FCSTD DOCUMENT  (FreeCAD 0.20R29603 (Git))
Label: layout
License: All rights reserved
LicenseURL: http://en.wikipedia.org/wiki/All_rights_reserved
objects: Sketcher::SketchObject×6
note: 6 computed .brp shape members not serialized (recipe doc carries the construction recipe); baked Part::Feature solids carry a one-line shape summary decoded from their .brp

FEATURE [Sketcher::SketchObject] Sketch  label="grid"
  FullyConstrained = true
  sketch-geometry (158):
    g0: LineSegment StartX=-9 StartY=8.5 StartZ=0 EndX=9 EndY=8.5 EndZ=0
    g1: LineSegment StartX=9 StartY=8.5 StartZ=0 EndX=9 EndY=-8.5 EndZ=0
    g2: LineSegment StartX=9 StartY=-8.5 StartZ=0 EndX=-9 EndY=-8.5 EndZ=0
    g3: LineSegment StartX=-9 StartY=-8.5 StartZ=0 EndX=-9 EndY=8.5 EndZ=0
    g4: LineSegment StartX=-28.0528 StartY=-14.2521 StartZ=0 EndX=-10.1213 EndY=-12.6833 EndZ=0
    g5: LineSegment StartX=-28.0528 StartY=-14.2521 StartZ=0 EndX=-29.5345 EndY=2.68325 EndZ=0
    g6: LineSegment StartX=-29.5345 StartY=2.68325 StartZ=0 EndX=-11.603 EndY=4.25206 EndZ=0
    g7: LineSegment StartX=-11.603 StartY=4.25206 StartZ=0 EndX=-10.1213 EndY=-12.6833 EndZ=0
    g8: GeomPoint X=-19.8279 Y=-5 Z=0
    g9: LineSegment StartX=9 StartY=25.5 StartZ=0 EndX=-9 EndY=25.5 EndZ=0
    g10: LineSegment StartX=-9 StartY=25.5 StartZ=0 EndX=-9 EndY=8.5 EndZ=0
    g11: LineSegment StartX=-9 StartY=8.5 StartZ=0 EndX=9 EndY=8.5 EndZ=0
    g12: LineSegment StartX=9 StartY=8.5 StartZ=0 EndX=9 EndY=25.5 EndZ=0
    g13: LineSegment StartX=-9 StartY=-8.5 StartZ=0 EndX=9 EndY=-8.5 EndZ=0
    g14: LineSegment StartX=9 StartY=-8.5 StartZ=0 EndX=9 EndY=-25.5 EndZ=0
    g15: LineSegment StartX=9 StartY=-25.5 StartZ=0 EndX=-9 EndY=-25.5 EndZ=0
    g16: LineSegment StartX=-9 StartY=-25.5 StartZ=0 EndX=-9 EndY=-8.5 EndZ=0
    g17: LineSegment StartX=-10.1213 StartY=-12.6833 StartZ=0 EndX=-8.63967 EndY=-29.6186 EndZ=0
    g18: LineSegment StartX=-8.63967 StartY=-29.6186 StartZ=0 EndX=-26.5712 EndY=-31.1874 EndZ=0
    g19: LineSegment StartX=-26.5712 StartY=-31.1874 StartZ=0 EndX=-28.0528 EndY=-14.2521 EndZ=0
    g20: LineSegment StartX=9 StartY=42.5 StartZ=0 EndX=-9 EndY=42.5 EndZ=0
    g21: LineSegment StartX=-9 StartY=42.5 StartZ=0 EndX=-9 EndY=25.5 EndZ=0
    g22: LineSegment StartX=-9 StartY=25.5 StartZ=0 EndX=9 EndY=25.5 EndZ=0
    g23: LineSegment StartX=9 StartY=25.5 StartZ=0 EndX=9 EndY=42.5 EndZ=0
    g24: LineSegment StartX=-11.603 StartY=4.25206 StartZ=0 EndX=-13.0846 EndY=21.1874 EndZ=0
    g25: LineSegment StartX=-13.0846 StartY=21.1874 StartZ=0 EndX=-31.0161 EndY=19.6186 EndZ=0
    g26: LineSegment StartX=-29.5345 StartY=2.68325 StartZ=0 EndX=-31.0161 EndY=19.6186 EndZ=0
    g27: LineSegment StartX=-13.0846 StartY=21.1874 StartZ=0 EndX=-14.5663 EndY=38.1227 EndZ=0
    g28: LineSegment StartX=-14.5663 StartY=38.1227 StartZ=0 EndX=-32.4978 EndY=36.5539 EndZ=0
    g29: LineSegment StartX=-32.4978 StartY=36.5539 StartZ=0 EndX=-31.0161 EndY=19.6186 EndZ=0
    g30: GeomPoint X=-22.7912 Y=28.8706 Z=0
    g31: GeomPoint X=-21.3095 Y=11.9353 Z=0
    g32: GeomPoint X=-18.3462 Y=-21.9353 Z=0
    g33: LineSegment StartX=11.603 StartY=4.25206 StartZ=0 EndX=29.5345 EndY=2.68325 EndZ=0
    g34: LineSegment StartX=29.5345 StartY=2.68325 StartZ=0 EndX=28.0528 EndY=-14.2521 EndZ=0
    g35: LineSegment StartX=28.0528 StartY=-14.2521 StartZ=0 EndX=10.1213 EndY=-12.6833 EndZ=0
    g36: LineSegment StartX=10.1213 StartY=-12.6833 StartZ=0 EndX=11.603 EndY=4.25206 EndZ=0
    g37: GeomPoint X=19.8279 Y=-5 Z=0
    g38: LineSegment StartX=28.0528 StartY=-14.2521 StartZ=0 EndX=26.5712 EndY=-31.1874 EndZ=0
    g39: LineSegment StartX=26.5712 StartY=-31.1874 StartZ=0 EndX=8.63967 EndY=-29.6186 EndZ=0
    g40: LineSegment StartX=8.63967 StartY=-29.6186 StartZ=0 EndX=10.1213 EndY=-12.6833 EndZ=0
    g41: GeomPoint X=18.3462 Y=-21.9353 Z=0
    g42: LineSegment StartX=29.5345 StartY=2.68325 StartZ=0 EndX=31.0161 EndY=19.6186 EndZ=0
    g43: LineSegment StartX=31.0161 StartY=19.6186 StartZ=0 EndX=13.0846 EndY=21.1874 EndZ=0
    g44: LineSegment StartX=13.0846 StartY=21.1874 StartZ=0 EndX=11.603 EndY=4.25206 EndZ=0
    g45: GeomPoint X=21.3095 Y=11.9353 Z=0
    g46: LineSegment StartX=31.0161 StartY=19.6186 StartZ=0 EndX=32.4978 EndY=36.5539 EndZ=0
    g47: LineSegment StartX=32.4978 StartY=36.5539 StartZ=0 EndX=14.5663 EndY=38.1227 EndZ=0
    g48: LineSegment StartX=14.5663 StartY=38.1227 StartZ=0 EndX=13.0846 EndY=21.1874 EndZ=0
    g49: GeomPoint X=22.7912 Y=28.8706 Z=0
    g50: LineSegment StartX=-26.5712 StartY=-31.1874 StartZ=0 EndX=-44.5027 EndY=-32.7562 EndZ=0
    g51: LineSegment StartX=-44.5027 StartY=-32.7562 StartZ=0 EndX=-45.9843 EndY=-15.8209 EndZ=0
    g52: LineSegment StartX=-45.9843 StartY=-15.8209 StartZ=0 EndX=-28.0528 EndY=-14.2521 EndZ=0
    g53: GeomPoint X=-36.2778 Y=-23.5041 Z=0
    g54: LineSegment StartX=-29.5345 StartY=2.68325 StartZ=0 EndX=-47.466 EndY=1.11445 EndZ=0
    g55: LineSegment StartX=-47.466 StartY=1.11445 StartZ=0 EndX=-45.9843 EndY=-15.8209 EndZ=0
    g56: LineSegment StartX=-31.0161 StartY=19.6186 StartZ=0 EndX=-48.9476 EndY=18.0498 EndZ=0
    g57: LineSegment StartX=-48.9476 StartY=18.0498 StartZ=0 EndX=-47.466 EndY=1.11445 EndZ=0
    g58: LineSegment StartX=-48.9476 StartY=18.0498 StartZ=0 EndX=-50.4293 EndY=34.9851 EndZ=0
    g59: LineSegment StartX=-50.4293 StartY=34.9851 StartZ=0 EndX=-32.4978 EndY=36.5539 EndZ=0
    g60: GeomPoint X=-40.7227 Y=27.3018 Z=0
    g61: GeomPoint X=-39.241 Y=10.3665 Z=0
    g62: GeomPoint X=-37.7594 Y=-6.5688 Z=0
    g63: LineSegment StartX=30.8244 StartY=-7.0663 StartZ=0 EndX=27.8724 EndY=-23.808 EndZ=0
    g64: LineSegment StartX=27.8724 StartY=-23.808 StartZ=0 EndX=45.5989 EndY=-26.9337 EndZ=0
    g65: LineSegment StartX=45.5989 StartY=-26.9337 StartZ=0 EndX=48.5509 EndY=-10.192 EndZ=0
    g66: LineSegment StartX=48.5509 StartY=-10.192 StartZ=0 EndX=30.8244 EndY=-7.0663 EndZ=0
    g67: GeomPoint X=38.2116 Y=-17 Z=0
    g68: LineSegment StartX=45.5989 StartY=-26.9337 StartZ=0 EndX=42.6469 EndY=-43.6754 EndZ=0
    g69: LineSegment StartX=42.6469 StartY=-43.6754 StartZ=0 EndX=24.9203 EndY=-40.5498 EndZ=0
    g70: LineSegment StartX=24.9203 StartY=-40.5498 StartZ=0 EndX=27.8724 EndY=-23.808 EndZ=0
    g71: GeomPoint X=35.2596 Y=-33.7417 Z=0
    g72: LineSegment StartX=48.5509 StartY=-10.192 StartZ=0 EndX=51.5029 EndY=6.54976 EndZ=0
    g73: LineSegment StartX=51.5029 StartY=6.54976 StartZ=0 EndX=33.7764 EndY=9.67543 EndZ=0
    g74: LineSegment StartX=33.7764 StartY=9.67543 StartZ=0 EndX=30.8244 EndY=-7.0663 EndZ=0
    g75: GeomPoint X=41.1637 Y=-0.258268 Z=0
    g76: LineSegment StartX=51.5029 StartY=6.54976 StartZ=0 EndX=54.4549 EndY=23.2915 EndZ=0
    g77: LineSegment StartX=54.4549 StartY=23.2915 StartZ=0 EndX=36.7284 EndY=26.4172 EndZ=0
    g78: LineSegment StartX=36.7284 StartY=26.4172 StartZ=0 EndX=33.7764 EndY=9.67543 EndZ=0
    g79: GeomPoint X=44.1157 Y=16.4835 Z=0
    g80: LineSegment StartX=42.6469 StartY=-43.6754 StartZ=0 EndX=60.3734 EndY=-46.8011 EndZ=0
    g81: LineSegment StartX=60.3734 StartY=-46.8011 StartZ=0 EndX=63.3254 EndY=-30.0594 EndZ=0
    g82: LineSegment StartX=63.3254 StartY=-30.0594 StartZ=0 EndX=45.5989 EndY=-26.9337 EndZ=0
    g83: GeomPoint X=52.9862 Y=-36.8674 Z=0
    g84: LineSegment StartX=63.3254 StartY=-30.0594 StartZ=0 EndX=66.2775 EndY=-13.3176 EndZ=0
    g85: LineSegment StartX=48.5509 StartY=-10.192 StartZ=0 EndX=66.2775 EndY=-13.3176 EndZ=0
    g86: GeomPoint X=55.9382 Y=-20.1257 Z=0
    g87: LineSegment StartX=66.2775 StartY=-13.3176 StartZ=0 EndX=69.2295 EndY=3.4241 EndZ=0
    g88: LineSegment StartX=69.2295 StartY=3.4241 StartZ=0 EndX=51.5029 EndY=6.54976 EndZ=0
    g89: LineSegment StartX=72.1815 StartY=20.1658 StartZ=0 EndX=54.4549 EndY=23.2915 EndZ=0
    g90: GeomPoint X=58.8902 Y=-3.38394 Z=0
    g91: GeomPoint X=61.8422 Y=13.3578 Z=0
    g92: GeomPoint X=80.4064 Y=10.9138 Z=0
    g93: GeomPoint X=78.9248 Y=-6.02154 Z=0
    g94: LineSegment StartX=108.044 StartY=17.0282 StartZ=0 EndX=106.563 EndY=0.0929121 EndZ=0
    g95: GeomPoint X=98.3379 Y=9.34497 Z=0
    g96: GeomPoint X=96.8563 Y=-7.59034 Z=0
    g97: LineSegment StartX=-20.4485 StartY=-30.846 StartZ=0 EndX=-37.8352 EndY=-35.5048 EndZ=0
    g98: LineSegment StartX=-37.8352 StartY=-35.5048 StartZ=0 EndX=-33.4353 EndY=-51.9255 EndZ=0
    g99: LineSegment StartX=-33.4353 StartY=-51.9255 StartZ=0 EndX=-16.0486 EndY=-47.2668 EndZ=0
    g100: LineSegment StartX=-16.0486 StartY=-47.2668 StartZ=0 EndX=-20.4485 EndY=-30.846 EndZ=0
    g101: LineSegment StartX=-41.9353 StartY=-37.2031 StartZ=0 EndX=-57.5237 EndY=-46.2031 EndZ=0
    g102: LineSegment StartX=-57.5237 StartY=-46.2031 StartZ=0 EndX=-49.0237 EndY=-60.9255 EndZ=0
    g103: LineSegment StartX=-49.0237 StartY=-60.9255 StartZ=0 EndX=-33.4353 EndY=-51.9255 EndZ=0
    g104: LineSegment StartX=-33.4353 StartY=-51.9255 StartZ=0 EndX=-41.9353 EndY=-37.2031 EndZ=0
    g105: LineSegment StartX=-16.0486 StartY=-30.2668 StartZ=0 EndX=1.9514 EndY=-30.2668 EndZ=0
    g106: LineSegment StartX=-16.0486 StartY=-47.2668 StartZ=0 EndX=-16.0486 EndY=-30.2668 EndZ=0
    g107: GeomPoint X=-26.9419 Y=-41.3858 Z=0
    g108: GeomPoint X=-45.4795 Y=-49.0643 Z=0
    g109: GeomPoint X=-53.9795 Y=-34.3419 Z=0
    g110: LineSegment StartX=-41.9353 StartY=-37.2031 StartZ=0 EndX=-50.4353 EndY=-22.4806 EndZ=0
    g111: LineSegment StartX=-50.4353 StartY=-22.4806 StartZ=0 EndX=-66.0237 EndY=-31.4806 EndZ=0
    g112: LineSegment StartX=-66.0237 StartY=-31.4806 StartZ=0 EndX=-57.5237 EndY=-46.2031 EndZ=0
    g113: LineSegment StartX=1.9514 StartY=-47.2668 StartZ=0 EndX=-16.0486 EndY=-47.2668 EndZ=0
    g114: LineSegment StartX=72.1815 StartY=20.1658 StartZ=0 EndX=69.2295 EndY=3.4241 EndZ=0
    g115: LineSegment StartX=72.1815 StartY=20.1658 StartZ=0 EndX=90.113 EndY=18.597 EndZ=0
    g116: LineSegment StartX=72.1815 StartY=20.1658 StartZ=0 EndX=70.6998 EndY=3.23052 EndZ=0
    g117: LineSegment StartX=90.113 StartY=18.597 StartZ=0 EndX=88.6313 EndY=1.66172 EndZ=0
    g118: LineSegment StartX=88.6313 StartY=1.66172 StartZ=0 EndX=70.6998 EndY=3.23052 EndZ=0
    g119: LineSegment StartX=108.044 StartY=17.0282 StartZ=0 EndX=90.113 EndY=18.597 EndZ=0
    g120: LineSegment StartX=106.563 StartY=0.0929121 StartZ=0 EndX=88.6313 EndY=1.66172 EndZ=0
    g121: LineSegment StartX=108.044 StartY=17.0282 StartZ=0 EndX=125.976 EndY=15.4594 EndZ=0
    g122: LineSegment StartX=125.976 StartY=15.4594 StartZ=0 EndX=124.494 EndY=-1.47589 EndZ=0
    g123: LineSegment StartX=124.494 StartY=-1.47589 StartZ=0 EndX=106.563 EndY=0.0929121 EndZ=0
    g124: GeomPoint X=116.269 Y=7.77617 Z=0
    g125: LineSegment StartX=70.6998 StartY=3.23052 StartZ=0 EndX=69.2182 EndY=-13.7048 EndZ=0
    g126: LineSegment StartX=88.6313 StartY=1.66172 StartZ=0 EndX=87.1497 EndY=-15.2736 EndZ=0
    g127: LineSegment StartX=87.1497 StartY=-15.2736 StartZ=0 EndX=69.2182 EndY=-13.7048 EndZ=0
    g128: LineSegment StartX=106.563 StartY=0.0929121 StartZ=0 EndX=105.081 EndY=-16.8424 EndZ=0
    g129: LineSegment StartX=105.081 StartY=-16.8424 StartZ=0 EndX=87.1497 EndY=-15.2736 EndZ=0
    g130: LineSegment StartX=124.494 StartY=-1.47589 StartZ=0 EndX=123.013 EndY=-18.4112 EndZ=0
    g131: LineSegment StartX=123.013 StartY=-18.4112 StartZ=0 EndX=105.081 EndY=-16.8424 EndZ=0
    g132: GeomPoint X=114.788 Y=-9.15914 Z=0
    g133: LineSegment StartX=69.2182 StartY=-13.7048 StartZ=0 EndX=67.7365 EndY=-30.6401 EndZ=0
    g134: LineSegment StartX=67.7365 StartY=-30.6401 StartZ=0 EndX=85.6681 EndY=-32.2089 EndZ=0
    g135: LineSegment StartX=87.1497 StartY=-15.2736 StartZ=0 EndX=85.6681 EndY=-32.2089 EndZ=0
    g136: LineSegment StartX=105.081 StartY=-16.8424 StartZ=0 EndX=103.6 EndY=-33.7777 EndZ=0
    g137: LineSegment StartX=103.6 StartY=-33.7777 StartZ=0 EndX=85.6681 EndY=-32.2089 EndZ=0
    g138: LineSegment StartX=123.013 StartY=-18.4112 StartZ=0 EndX=121.531 EndY=-35.3465 EndZ=0
    g139: LineSegment StartX=121.531 StartY=-35.3465 StartZ=0 EndX=103.6 EndY=-33.7777 EndZ=0
    g140: GeomPoint X=113.306 Y=-26.0945 Z=0
    g141: GeomPoint X=95.3746 Y=-24.5257 Z=0
    g142: GeomPoint X=77.4431 Y=-22.9568 Z=0
    g143: LineSegment StartX=67.7365 StartY=-30.6401 StartZ=0 EndX=66.2549 EndY=-47.5754 EndZ=0
    g144: LineSegment StartX=85.6681 StartY=-32.2089 StartZ=0 EndX=84.1864 EndY=-49.1442 EndZ=0
    g145: LineSegment StartX=66.2549 StartY=-47.5754 StartZ=0 EndX=84.1864 EndY=-49.1442 EndZ=0
    g146: LineSegment StartX=103.6 StartY=-33.7777 StartZ=0 EndX=102.118 EndY=-50.713 EndZ=0
    g147: LineSegment StartX=102.118 StartY=-50.713 StartZ=0 EndX=84.1864 EndY=-49.1442 EndZ=0
    g148: LineSegment StartX=102.118 StartY=-50.713 StartZ=0 EndX=120.049 EndY=-52.2818 EndZ=0
    g149: LineSegment StartX=121.531 StartY=-35.3465 StartZ=0 EndX=120.049 EndY=-52.2818 EndZ=0
    g150: GeomPoint X=75.9615 Y=-39.8922 Z=0
    g151: GeomPoint X=93.893 Y=-41.461 Z=0
    g152: GeomPoint X=111.824 Y=-43.0298 Z=0
    g153: GeomPoint X=-1e-16 Y=17 Z=0
    g154: GeomPoint X=7e-16 Y=34 Z=0
    g155: GeomPoint X=-2e-16 Y=-17 Z=0
    g156: LineSegment StartX=1.9514 StartY=-47.2668 StartZ=0 EndX=1.9514 EndY=-30.2668 EndZ=0
    g157: GeomPoint X=-7.0486 Y=-38.7668 Z=0
  constraints (360):
    c: Coincident(g0,g1)
    c: Coincident(g1,g2)
    c: Coincident(g2,g3)
    c: Coincident(g3,g0)
    c: Horizontal(g0)
    c: Horizontal(g2)
    c: Vertical(g1)
    c: Vertical(g3)
    c: Distance(g0) = 18
    c: Distance(g1) = 17
    c: Symmetric(g0,g1,g-1)
    c: Coincident(g5,g4)
    c: Coincident(g6,g5)
    c: Coincident(g7,g6)
    c: Coincident(g7,g4)
    c: Perpendicular(g4,g5)
    c: Perpendicular(g4,g7)
    c: Perpendicular(g6,g7)
    c: Distance(g4) = 18
    c: Distance(g7) = 17
    c: Symmetric(g4,g5,g8)
    c: DistanceY(g8,g-1) = 5
    c: Angle(g4,g0) = -0.0872665
    c: Coincident(g9,g10)
    c: Coincident(g10,g11)
    c: Coincident(g11,g12)
    c: Coincident(g12,g9)
    c: Horizontal(g9)
    c: Horizontal(g11)
    c: Vertical(g10)
    c: Vertical(g12)
    c: DistanceX(g9,g9) = 18
    c: DistanceY(g12,g12) = 17
    c: Coincident(g10,g0)
    c: Coincident(g13,g14)
    c: Coincident(g14,g15)
    c: Coincident(g15,g16)
    c: Coincident(g16,g13)
    c: Horizontal(g13)
    c: Horizontal(g15)
    c: Vertical(g14)
    c: Vertical(g16)
    c: DistanceX(g13,g13) = 18
    c: DistanceY(g14,g14) = 17
    c: Coincident(g2,g13)
    c: Coincident(g17,g4)
    c: Distance(g17) = 17
    c: Perpendicular(g17,g4)
    c: Coincident(g18,g17)
    c: Coincident(g19,g18)
    c: Coincident(g19,g4)
    c: Perpendicular(g19,g4)
    c: Perpendicular(g18,g19)
    c: Coincident(g20,g21)
    c: Coincident(g21,g22)
    c: Coincident(g22,g23)
    c: Coincident(g23,g20)
    c: Horizontal(g20)
    c: Horizontal(g22)
    c: Vertical(g21)
    c: Vertical(g23)
    c: DistanceX(g20,g20) = 18
    c: DistanceY(g23,g23) = 17
    c: Coincident(g22,g9)
    c: Coincident(g24,g6)
    c: Coincident(g25,g24)
    c: Coincident(g26,g5)
    c: Coincident(g26,g25)
    c: Perpendicular(g6,g26)
    c: Perpendicular(g25,g24)
    c: Distance(g24) = 17
    c: Perpendicular(g6,g24)
    c: Coincident(g27,g24)
    c: Coincident(g28,g27)
    c: Coincident(g29,g28)
    c: Coincident(g29,g25)
    c: Perpendicular(g25,g27)
    c: Perpendicular(g29,g25)
    c: Perpendicular(g28,g29)
    c: Distance(g27) = 17
    c: PointOnObject(g15,g17)
    c: Symmetric(g28,g24,g30)
    c: Symmetric(g25,g6,g31)
    c: Symmetric(g4,g17,g32)
    c: Coincident(g34,g33)
    c: Coincident(g35,g34)
    c: Coincident(g36,g35)
    c: Coincident(g36,g33)
    c: Angle(g33,g0) = 0.0872665
    c: Perpendicular(g34,g33)
    c: Perpendicular(g36,g33)
    c: Perpendicular(g35,g36)
    c: Distance(g33) = 18
    c: Distance(g34) = 17
    c: Symmetric(g33,g34,g37)
    c: DistanceY(g-1,g37) = -5
    c: Coincident(g38,g34)
    c: Coincident(g39,g38)
    c: Coincident(g40,g39)
    c: Coincident(g40,g35)
    c: Perpendicular(g38,g35)
    c: Perpendicular(g40,g35)
    c: Perpendicular(g39,g40)
    c: Distance(g40) = 17
    c: PointOnObject(g14,g40)
    c: Symmetric(g35,g38,g41)
    c: Coincident(g42,g33)
    c: Coincident(g43,g42)
    c: Coincident(g44,g43)
    c: Coincident(g44,g33)
    c: Distance(g42) = 17
    c: Perpendicular(g33,g42)
    c: Perpendicular(g44,g33)
    c: Perpendicular(g43,g44)
    c: Symmetric(g43,g33,g45)
    c: Coincident(g46,g42)
    c: Coincident(g47,g46)
    c: Coincident(g48,g47)
    c: Coincident(g48,g43)
    c: Distance(g46) = 17
    c: Perpendicular(g43,g46)
    c: Perpendicular(g48,g43)
    c: Perpendicular(g47,g48)
    c: Symmetric(g47,g42,g49)
    c: Coincident(g50,g18)
    c: Coincident(g51,g50)
    c: Coincident(g52,g51)
    c: Coincident(g52,g4)
    c: Distance(g51) = 17
    c: Perpendicular(g50,g51)
    c: Symmetric(g51,g18,g53)
    c: Coincident(g54,g5)
    c: Coincident(g55,g54)
    c: Coincident(g55,g51)
    c: Perpendicular(g54,g5)
    c: Perpendicular(g55,g54)
    c: Coincident(g56,g25)
    c: Coincident(g57,g56)
    c: Coincident(g57,g54)
    c: Coincident(g58,g56)
    c: Perpendicular(g54,g57)
    c: Perpendicular(g56,g26)
    c: Perpendicular(g58,g56)
    c: Coincident(g58,g59)
    c: Perpendicular(g58,g59)
    c: Coincident(g59,g28)
    c: Symmetric(g58,g25,g60)
    c: Symmetric(g56,g5,g61)
    c: Symmetric(g54,g4,g62)
    c: Coincident(g64,g63)
    c: Coincident(g65,g64)
    c: Coincident(g66,g65)
    c: Coincident(g66,g63)
    c: Distance(g66) = 18
    c: Distance(g65) = 17
    c: Perpendicular(g65,g66)
    c: Perpendicular(g64,g65)
    c: Perpendicular(g63,g64)
    c: Symmetric(g63,g64,g67)
    c: DistanceY(g67,g37) = 12
    c: Coincident(g68,g64)
    c: Coincident(g69,g68)
    c: Coincident(g70,g69)
    c: Coincident(g70,g63)
    c: Distance(g68) = 17
    c: Perpendicular(g68,g64)
    c: Perpendicular(g70,g64)
    c: Perpendicular(g69,g68)
    c: PointOnObject(g38,g70)
    c: Symmetric(g63,g68,g71)
    c: Coincident(g72,g65)
    c: Coincident(g73,g72)
    c: Coincident(g74,g73)
    c: Coincident(g74,g63)
    c: Perpendicular(g66,g72)
    c: Perpendicular(g74,g66)
    c: Perpendicular(g73,g72)
    c: Distance(g72) = 17
    c: Symmetric(g73,g65,g75)
    c: Coincident(g76,g72)
    c: Coincident(g77,g76)
    c: Coincident(g78,g77)
    c: Coincident(g78,g73)
    c: Distance(g76) = 17
    c: Perpendicular(g73,g76)
    c: Perpendicular(g78,g73)
    c: Perpendicular(g76,g77)
    c: Symmetric(g77,g72,g79)
    c: Coincident(g80,g68)
    c: Distance(g80) = 18
    c: Perpendicular(g80,g68)
    c: Coincident(g81,g80)
    c: Coincident(g82,g81)
    c: Coincident(g82,g64)
    c: Perpendicular(g68,g82)
    c: Perpendicular(g80,g81)
    c: Symmetric(g64,g80,g83)
    c: Coincident(g84,g81)
    c: Perpendicular(g84,g82)
    c: Coincident(g85,g65)
    c: Coincident(g85,g84)
    c: Perpendicular(g65,g85)
    c: Symmetric(g65,g81,g86)
    c: Coincident(g87,g84)
    c: Coincident(g88,g87)
    c: Coincident(g88,g72)
    c: Perpendicular(g85,g87)
    c: Perpendicular(g72,g88)
    c: Coincident(g89,g76)
    c: Perpendicular(g76,g89)
    c: Symmetric(g72,g84,g90)
    c: Symmetric(g76,g87,g91)
    c: Coincident(g98,g97)
    c: Coincident(g99,g98)
    c: Coincident(g100,g99)
    c: Coincident(g100,g97)
    c: Perpendicular(g97,g100)
    c: Perpendicular(g98,g97)
    c: Perpendicular(g98,g99)
    c: Distance(g97) = 18
    c: Distance(g100) = 17
    c: Coincident(g102,g101)
    c: Coincident(g103,g102)
    c: Coincident(g104,g103)
    c: Coincident(g104,g101)
    c: Perpendicular(g102,g101)
    c: Perpendicular(g104,g101)
    c: Perpendicular(g103,g104)
    c: Distance(g101) = 18
    c: Distance(g104) = 17
    c: Coincident(g106,g105)
    c: Horizontal(g105)
    c: Vertical(g106)
    c: Distance(g105) = 18
    c: Coincident(g98,g103)
    c: Angle(g106,g100) = 0.261799
    c: Angle(g104,g98) = -0.261799
    c: Coincident(g110,g101)
    c: Coincident(g111,g110)
    c: Coincident(g112,g111)
    c: Coincident(g112,g101)
    c: Symmetric(g99,g97,g107)
    c: Symmetric(g98,g101,g108)
    c: Symmetric(g101,g111,g109)
    c: Perpendicular(g101,g110)
    c: Perpendicular(g112,g101)
    c: Perpendicular(g111,g112)
    c: Distance(g110) = 17
    c: Coincident(g113,g99)
    c: Horizontal(g113)
    c: Distance(g52) = 18
    c: Perpendicular(g52,g5)
    c: Equal(g113,g105)
    c: Coincident(g114,g89)
    c: Coincident(g114,g87)
    c: Perpendicular(g114,g88)
    c: Coincident(g115,g89)
    c: Coincident(g116,g89)
    c: Angle(g114,g116) = 0.0872665
    c: Distance(g115) = 18
    c: Distance(g116) = 17
    c: Coincident(g117,g115)
    c: Coincident(g118,g117)
    c: Coincident(g118,g116)
    c: Perpendicular(g116,g115)
    c: Perpendicular(g117,g115)
    c: Perpendicular(g118,g116)
    c: Coincident(g119,g94)
    c: Coincident(g119,g115)
    c: Perpendicular(g117,g119)
    c: Perpendicular(g94,g119)
    c: Distance(g119) = 18
    c: Symmetric(g89,g117,g92)
    c: Symmetric(g115,g94,g95)
    c: Coincident(g120,g94)
    c: Coincident(g120,g117)
    c: Perpendicular(g120,g117)
    c: Coincident(g121,g94)
    c: Coincident(g122,g121)
    c: Coincident(g123,g122)
    c: Coincident(g123,g94)
    c: Distance(g121) = 18
    c: Perpendicular(g94,g121)
    c: Perpendicular(g123,g94)
    c: Perpendicular(g122,g123)
    c: Symmetric(g94,g122,g124)
    c: Coincident(g125,g116)
    c: Distance(g125) = 17
    c: Perpendicular(g118,g125)
    c: Coincident(g126,g117)
    c: Coincident(g127,g126)
    c: Coincident(g127,g125)
    c: Perpendicular(g126,g118)
    c: Perpendicular(g127,g125)
    c: Symmetric(g116,g126,g93)
    c: Coincident(g128,g94)
    c: Coincident(g129,g128)
    c: Coincident(g129,g126)
    c: Perpendicular(g128,g120)
    c: Perpendicular(g129,g126)
    c: Symmetric(g117,g128,g96)
    c: Coincident(g130,g122)
    c: Perpendicular(g130,g123)
    c: Coincident(g131,g130)
    c: Coincident(g131,g128)
    c: Perpendicular(g131,g128)
    c: Symmetric(g94,g130,g132)
    c: Coincident(g133,g125)
    c: Coincident(g134,g133)
    c: Coincident(g135,g126)
    c: Coincident(g135,g134)
    c: Coincident(g136,g128)
    c: Coincident(g137,g136)
    c: Coincident(g137,g134)
    c: Coincident(g138,g130)
    c: Coincident(g139,g138)
    c: Coincident(g139,g136)
    c: Distance(g133) = 17
    c: Perpendicular(g127,g133)
    c: Perpendicular(g134,g135)
    c: Perpendicular(g127,g135)
    c: Perpendicular(g129,g136)
    c: Perpendicular(g137,g136)
    c: Perpendicular(g138,g131)
    c: Perpendicular(g139,g136)
    c: Symmetric(g125,g134,g142)
    c: Symmetric(g126,g136,g141)
    c: Symmetric(g128,g138,g140)
    c: Coincident(g143,g133)
    c: Coincident(g144,g134)
    c: Coincident(g145,g143)
    c: Coincident(g145,g144)
    c: Coincident(g146,g136)
    c: Coincident(g147,g146)
    c: Coincident(g147,g144)
    c: Coincident(g148,g146)
    c: Coincident(g149,g138)
    c: Coincident(g149,g148)
    c: Distance(g143) = 17
    c: Perpendicular(g143,g134)
    c: Perpendicular(g145,g143)
    c: Perpendicular(g144,g134)
    c: Perpendicular(g146,g137)
    c: Perpendicular(g147,g144)
    c: Perpendicular(g149,g139)
    c: Perpendicular(g148,g146)
    c: Symmetric(g133,g144,g150)
    c: Symmetric(g134,g146,g151)
    c: Symmetric(g136,g148,g152)
    c: Symmetric(g2,g14,g155)
    c: Symmetric(g9,g0,g153)
    c: Symmetric(g20,g9,g154)
    c: PointOnObject(g50,g110)
    c: PointOnObject(g105,g18)
    c: Coincident(g156,g113)
    c: Symmetric(g105,g113,g157)
    c: Coincident(g105,g156)
    c: Coincident(g106,g99)
    c: Distance(g156) = 17
    c: Angle(g63,g38) = 0.0872665
FEATURE [Sketcher::SketchObject] Sketch002  label="mid"
  FullyConstrained = true
  sketch-geometry (83):
    g0: GeomPoint X=-19.8279 Y=-5 Z=0
    g1: LineSegment StartX=9 StartY=-25.5 StartZ=0 EndX=-9 EndY=-25.5 EndZ=0
    g2: GeomPoint X=19.8279 Y=-5 Z=0
    g3: LineSegment StartX=26.5712 StartY=-31.1874 StartZ=0 EndX=8.63967 EndY=-29.6186 EndZ=0
    g4: LineSegment StartX=31.0161 StartY=19.6186 StartZ=0 EndX=13.0846 EndY=21.1874 EndZ=0
    g5: GeomPoint X=38.2116 Y=-17 Z=0
    g6: LineSegment StartX=60.3734 StartY=-46.8011 StartZ=0 EndX=24.9203 EndY=-40.5498 EndZ=0
    g7: LineSegment StartX=36.7284 StartY=26.4172 StartZ=0 EndX=72.1815 EndY=20.1658 EndZ=0
    g8: LineSegment StartX=13.0846 StartY=21.1874 StartZ=0 EndX=8.63967 EndY=-29.6186 EndZ=0
    g9: LineSegment StartX=26.5712 StartY=-31.1874 StartZ=0 EndX=31.0161 EndY=19.6186 EndZ=0
    g10: LineSegment StartX=-13.0846 StartY=21.1874 StartZ=0 EndX=-8.63967 EndY=-29.6186 EndZ=0
    g11: LineSegment StartX=-48.9476 StartY=18.0498 StartZ=0 EndX=-44.5027 EndY=-32.7562 EndZ=0
    g12: LineSegment StartX=-8.63967 StartY=-29.6186 StartZ=0 EndX=-44.5027 EndY=-32.7562 EndZ=0
    g13: GeomPoint X=-28.7936 Y=-5.7844 Z=0
    g14: GeomPoint X=-10.8621 Y=-4.2156 Z=0
    g15: LineSegment StartX=-9 StartY=25.5 StartZ=0 EndX=-9 EndY=-25.5 EndZ=0
    g16: LineSegment StartX=9 StartY=-25.5 StartZ=0 EndX=9 EndY=25.5 EndZ=0
    g17: LineSegment StartX=36.7284 StartY=26.4172 StartZ=0 EndX=24.9203 EndY=-40.5498 EndZ=0
    g18: LineSegment StartX=72.1815 StartY=20.1658 StartZ=0 EndX=60.3734 EndY=-46.8011 EndZ=0
    g19: GeomPoint X=45.5989 Y=-26.9337 Z=0
    g20: GeomPoint X=30.8244 Y=-7.0663 Z=0
    g21: GeomPoint X=36.9021 Y=27.402 Z=0
    g22: LineSegment StartX=35.7436 StartY=26.5908 StartZ=0 EndX=34.7484 EndY=20.9469 EndZ=0
    g23: GeomPoint X=35.7332 Y=20.7733 Z=0
    g24: LineSegment StartX=35.7332 StartY=20.7733 StartZ=0 EndX=34.7484 EndY=20.9469 EndZ=0
    g25: GeomPoint X=-49.2091 Y=21.0383 Z=0
    g26: LineSegment StartX=-48.9476 StartY=18.0498 StartZ=0 EndX=-49.2091 EndY=21.0383 EndZ=0
    g27: LineSegment StartX=36.9021 StartY=27.402 StartZ=0 EndX=72.3551 EndY=21.1506 EndZ=0
    g28: LineSegment StartX=10 StartY=25.5 StartZ=0 EndX=10 EndY=23.1283 EndZ=0
    g29: LineSegment StartX=9 StartY=26.5 StartZ=0 EndX=-9 EndY=26.5 EndZ=0
    g30: GeomPoint X=0 Y=26.5 Z=0
    g31: ArcOfCircle CenterX=3 CenterY=27.5 CenterZ=0 NormalX=0 NormalY=0 NormalZ=1 AngleXU=0 Radius=1 StartAngle=1.5708 EndAngle=4.71239
    g32: ArcOfCircle CenterX=-3 CenterY=27.5 CenterZ=0 NormalX=0 NormalY=0 NormalZ=1 AngleXU=0 Radius=1 StartAngle=4.71239 EndAngle=7.85398
    g33: LineSegment StartX=-12 StartY=27.5 StartZ=0 EndX=-12 EndY=25.0367 EndZ=0
    g34: LineSegment StartX=-10 StartY=25.5 StartZ=0 EndX=-10 EndY=23.1283 EndZ=0
    g35: LineSegment StartX=3 StartY=28.5 StartZ=0 EndX=11 EndY=28.5 EndZ=0
    g36: LineSegment StartX=-3 StartY=28.5 StartZ=0 EndX=-11 EndY=28.5 EndZ=0
    g37: LineSegment StartX=-22.3118 StartY=23.3915 StartZ=0 EndX=-49.2091 EndY=21.0383 EndZ=0
    g38: LineSegment StartX=3 StartY=27.5 StartZ=0 EndX=-3 EndY=27.5 EndZ=0
    g39: LineSegment StartX=-37.1676 StartY=21.088 StartZ=0 EndX=-43.1448 EndY=20.5651 EndZ=0
    g40: ArcOfCircle CenterX=-37.1676 CenterY=21.088 CenterZ=0 NormalX=0 NormalY=0 NormalZ=1 AngleXU=0 Radius=1 StartAngle=1.65806 EndAngle=4.79966
    g41: ArcOfCircle CenterX=-43.1448 CenterY=20.5651 CenterZ=0 NormalX=0 NormalY=0 NormalZ=1 AngleXU=0 Radius=1 StartAngle=4.79966 EndAngle=7.94125
    g42: LineSegment StartX=9 StartY=25.5 StartZ=0 EndX=-9 EndY=25.5 EndZ=0
    g43: GeomPoint X=-22.0504 Y=20.403 Z=0
    g44: LineSegment StartX=-22.0504 StartY=20.403 StartZ=0 EndX=-22.3118 EndY=23.3915 EndZ=0
    g45: ArcOfCircle CenterX=8.4e-15 CenterY=-231.634 CenterZ=0 NormalX=0 NormalY=0 NormalZ=1 AngleXU=0 Radius=254 StartAngle=1.438 EndAngle=1.65806
    g46: ArcOfCircle CenterX=8.4e-15 CenterY=-231.634 CenterZ=0 NormalX=0 NormalY=0 NormalZ=1 AngleXU=0 Radius=256 StartAngle=1.44837 EndAngle=1.65806
    g47: LineSegment StartX=-22.1375 StartY=21.3992 StartZ=0 EndX=-49.0348 EndY=19.046 EndZ=0
    g48: LineSegment StartX=-13.0846 StartY=21.1874 StartZ=0 EndX=-48.9476 EndY=18.0498 EndZ=0
    g49: GeomPoint X=-31.0161 Y=19.6186 Z=0
    g50: GeomPoint X=0 Y=27.5 Z=0
    g51: LineSegment StartX=0 StartY=27.5 StartZ=0 EndX=0 EndY=26.5 EndZ=0
    g52: ArcOfCircle CenterX=-25.2133 CenterY=22.1339 CenterZ=0 NormalX=0 NormalY=0 NormalZ=1 AngleXU=0 Radius=1 StartAngle=4.79966 EndAngle=7.94125
    g53: LineSegment StartX=-22.2247 StartY=22.3954 StartZ=0 EndX=-25.2133 EndY=22.1339 EndZ=0
    g54: GeomPoint X=-40.1562 Y=20.8266 Z=0
    g55: GeomPoint X=-39.9819 Y=18.8342 Z=0
    g56: LineSegment StartX=-40.1562 StartY=20.8266 StartZ=0 EndX=-39.9819 EndY=18.8342 EndZ=0
    g57: ArcOfCircle CenterX=-19.2346 CenterY=22.6392 CenterZ=0 NormalX=0 NormalY=0 NormalZ=1 AngleXU=0 Radius=1 StartAngle=1.6463 EndAngle=4.78789
    g58: LineSegment StartX=-19.2346 StartY=22.6392 StartZ=0 EndX=7.1e-15 EndY=-231.634 EndZ=0
    g59: LineSegment StartX=8.4e-15 StartY=-231.634 StartZ=0 EndX=-22.2247 EndY=22.3954 EndZ=0
    g60: GeomPoint X=22.0504 Y=20.403 Z=0
    g61: LineSegment StartX=22.0504 StartY=20.403 StartZ=0 EndX=22.1375 EndY=21.3992 EndZ=0
    g62: ArcOfCircle CenterX=33.7636 CenterY=21.1206 CenterZ=0 NormalX=0 NormalY=0 NormalZ=1 AngleXU=0 Radius=1 StartAngle=4.57959 EndAngle=6.10865
    g63: ArcOfCircle CenterX=13 CenterY=25.0367 CenterZ=0 NormalX=0 NormalY=0 NormalZ=1 AngleXU=0 Radius=1 StartAngle=3.14159 EndAngle=4.66178
    g64: LineSegment StartX=12 StartY=27.5 StartZ=0 EndX=12 EndY=25.0367 EndZ=0
    g65: ArcOfCircle CenterX=11 CenterY=23.1283 CenterZ=0 NormalX=0 NormalY=0 NormalZ=1 AngleXU=0 Radius=1 StartAngle=3.14159 EndAngle=4.66924
    g66: ArcOfCircle CenterX=9 CenterY=25.5 CenterZ=0 NormalX=0 NormalY=0 NormalZ=1 AngleXU=0 Radius=1 StartAngle=-9e-16 EndAngle=1.5708
    g67: ArcOfCircle CenterX=-9 CenterY=25.5 CenterZ=0 NormalX=0 NormalY=0 NormalZ=1 AngleXU=0 Radius=1 StartAngle=1.5708 EndAngle=3.14159
    g68: ArcOfCircle CenterX=-11 CenterY=23.1283 CenterZ=0 NormalX=0 NormalY=0 NormalZ=1 AngleXU=0 Radius=1 StartAngle=4.75554 EndAngle=6.28319
    g69: ArcOfCircle CenterX=-13 CenterY=25.0367 CenterZ=0 NormalX=0 NormalY=0 NormalZ=1 AngleXU=0 Radius=1 StartAngle=4.76299 EndAngle=6.28319
    g70: LineSegment StartX=31.0161 StartY=19.6186 StartZ=0 EndX=31.2638 EndY=22.4495 EndZ=0
    g71: ArcOfCircle CenterX=19.2346 CenterY=22.6392 CenterZ=0 NormalX=0 NormalY=0 NormalZ=1 AngleXU=0 Radius=1 StartAngle=4.63689 EndAngle=7.77848
    g72: ArcOfCircle CenterX=25.2117 CenterY=22.1163 CenterZ=0 NormalX=0 NormalY=0 NormalZ=1 AngleXU=0 Radius=1 StartAngle=1.47176 EndAngle=4.61336
    g73: LineSegment StartX=-19.2346 StartY=22.6392 StartZ=0 EndX=-22.2247 EndY=22.3954 EndZ=0
    g74: LineSegment StartX=19.2346 StartY=22.6392 StartZ=0 EndX=22.2231 EndY=22.3778 EndZ=0
    g75: LineSegment StartX=22.2231 StartY=22.3778 StartZ=0 EndX=25.2117 EndY=22.1163 EndZ=0
    g76: LineSegment StartX=22.2231 StartY=22.3778 StartZ=0 EndX=22.1375 EndY=21.3992 EndZ=0
    g77: ArcOfCircle CenterX=-11 CenterY=27.5 CenterZ=0 NormalX=0 NormalY=0 NormalZ=1 AngleXU=0 Radius=1 StartAngle=1.5708 EndAngle=3.14159
    g78: ArcOfCircle CenterX=11 CenterY=27.5 CenterZ=0 NormalX=0 NormalY=0 NormalZ=1 AngleXU=0 Radius=1 StartAngle=1e-15 EndAngle=1.5708
    g79: LineSegment StartX=-10 StartY=25.5 StartZ=0 EndX=-12 EndY=25.5 EndZ=0
    g80: LineSegment StartX=12 StartY=25.0367 StartZ=0 EndX=10 EndY=25.0367 EndZ=0
    g81: ArcOfCircle CenterX=36.7284 CenterY=26.4172 CenterZ=0 NormalX=0 NormalY=0 NormalZ=1 AngleXU=0 Radius=1 StartAngle=1.39626 EndAngle=2.96706
    g82: LineSegment StartX=72.1815 StartY=20.1658 StartZ=0 EndX=72.3551 EndY=21.1506 EndZ=0
  constraints (192):
    c: DistanceY(g0,g-1) = 5
    c: Horizontal(g1)
    c: DistanceY(g-1,g2) = -5
    c: DistanceY(g5,g2) = 12
    c: Coincident(g8,g4)
    c: Coincident(g8,g3)
    c: Coincident(g9,g3)
    c: Coincident(g9,g4)
    c: PointOnObject(g1,g8)
    c: PointOnObject(g1,g10)
    c: Coincident(g12,g10)
    c: Coincident(g12,g11)
    c: Symmetric(g11,g10,g13)
    c: Symmetric(g10,g10,g14)
    c: Symmetric(g14,g13,g0)
    c: Distance(g12) = 36
    c: Perpendicular(g11,g12)
    c: Perpendicular(g8,g4)
    c: Perpendicular(g9,g4)
    c: Perpendicular(g9,g3)
    c: Symmetric(g4,g3,g2)
    c: Distance(g3) = 18
    c: Coincident(g15,g1)
    c: Vertical(g15)
    c: Coincident(g16,g1)
    c: Vertical(g16)
    c: Symmetric(g15,g1,g-1)
    c: Distance(g15) = 51
    c: Equal(g15,g10)
    c: Equal(g16,g8)
    c: Angle(g15,g10) = 0.0872665
    c: Angle(g8,g16) = 0.0872665
    c: Coincident(g17,g7)
    c: Coincident(g17,g6)
    c: Perpendicular(g6,g17)
    c: Coincident(g18,g6)
    c: Distance(g6) = 36
    c: Distance(g17) = 68
    c: Perpendicular(g18,g7)
    c: Perpendicular(g6,g18)
    c: Symmetric(g6,g7,g20)
    c: Symmetric(g19,g20,g5)
    c: PointOnObject(g3,g17)
    c: Angle(g17,g9) = 0.0872665
    c: PointOnObject(g23,g17)
    c: Coincident(g24,g23)
    c: Coincident(g24,g22)
    c: Distance(g24) = 1
    c: Perpendicular(g17,g24)
    c: Coincident(g26,g25)
    c: Coincident(g18,g7)
    c: Symmetric(g20,g6,g19)
    c: Symmetric(g29,g29,g30)
    c: Tangent(g32,g29) = 1.5708
    c: Tangent(g31,g29) = 1.5708
    c: Tangent(g36,g32) = -1.5708
    c: Coincident(g38,g32)
    c: Horizontal(g38)
    c: Coincident(g31,g38)
    c: Distance(g38) = 6
    c: Distance(g39) = 6
    c: Coincident(g40,g39)
    c: Tangent(g40,g37) = -1.5708
    c: Coincident(g41,g39)
    c: Tangent(g41,g37) = -1.5708
    c: Coincident(g26,g37)
    c: Distance(g26) = 3
    c: Tangent(g31,g35) = 1.5708
    c: Radius(g31) = 1
    c: Coincident(g27,g21)
    c: Coincident(g42,g16)
    c: Coincident(g42,g15)
    c: Horizontal(g42)
    c: Distance(g42) = 18
    c: Coincident(g44,g43)
    c: Coincident(g44,g37)
    c: Perpendicular(g37,g44)
    c: Coincident(g46,g37)
    c: Coincident(g46,g45)
    c: PointOnObject(g47,g26)
    c: Coincident(g11,g26)
    c: Tangent(g41,g47) = 1.5708
    c: Tangent(g40,g47) = 1.5708
    c: PointOnObject(g45,g44)
    c: Coincident(g48,g10)
    c: Coincident(g48,g11)
    c: Perpendicular(g11,g48)
    c: Perpendicular(g12,g10)
    c: Perpendicular(g48,g26)
    c: Perpendicular(g26,g37)
    c: Perpendicular(g26,g47)
    c: Symmetric(g11,g10,g49)
    c: Symmetric(g49,g10,g44)
    c: Tangent(g47,g45) = -1.5708
    c: Symmetric(g32,g31,g50)
    c: Coincident(g51,g50)
    c: Coincident(g51,g30)
    c: Vertical(g51)
    c: Tangent(g52,g37) = -1.5708
    c: Tangent(g52,g47) = 1.5708
    c: Coincident(g53,g52)
    c: Distance(g53) = 3
    c: Symmetric(g11,g49,g55)
    c: Symmetric(g39,g39,g54)
    c: Coincident(g56,g54)
    c: Coincident(g56,g55)
    c: Perpendicular(g56,g48)
    c: PointOnObject(g53,g44)
    c: Tangent(g57,g45) = 1.5708
    c: Tangent(g57,g46) = -1.5708
    c: Coincident(g58,g57)
    c: Coincident(g58,g45)
    c: Coincident(g59,g45)
    c: Coincident(g59,g53)
    c: Angle(g58,g59) = 0.0117647
    c: Radius(g57) = 1
    c: PointOnObject(g60,g4)
    c: Coincident(g61,g60)
    c: PointOnObject(g61,g45)
    c: Perpendicular(g4,g61)
    c: Perpendicular(g45,g61)
    c: Distance(g61) = 1
    c: Tangent(g62,g22) = 1.5708
    c: Radius(g62) = 1
    c: Radius(g63) = 1
    c: Tangent(g64,g63) = -1.5708
    c: Tangent(g63,g46) = 1.5708
    c: Tangent(g65,g45) = 1.5708
    c: Tangent(g65,g28) = -1.5708
    c: Radius(g65) = 1
    c: Coincident(g66,g16)
    c: Radius(g66) = 1
    c: Parallel(g64,g16)
    c: Parallel(g28,g16)
    c: Tangent(g66,g29) = -1.5708
    c: Tangent(g66,g28) = 1.5708
    c: Parallel(g29,g42)
    c: PointOnObject(g51,g-2)
    c: Coincident(g67,g15)
    c: Coincident(g67,g29)
    c: Tangent(g67,g34) = -1.5708
    c: Parallel(g34,g15)
    c: Parallel(g33,g34)
    c: Parallel(g36,g29)
    c: Tangent(g69,g33) = 1.5708
    c: Tangent(g69,g46) = 1.5708
    c: Tangent(g68,g45) = 1.5708
    c: Tangent(g68,g34) = 1.5708
    c: Radius(g69) = 1
    c: Radius(g68) = 1
    c: Coincident(g70,g4)
    c: Coincident(g70,g46)
    c: Perpendicular(g4,g70)
    c: Tangent(g71,g46) = -1.5708
    c: Tangent(g71,g45) = 1.5708
    c: Tangent(g72,g45) = 1.5708
    c: Tangent(g72,g46) = -1.5708
    c: Coincident(g73,g57)
    c: Coincident(g73,g53)
    c: Parallel(g53,g47)
    c: Coincident(g74,g71)
    c: Coincident(g75,g74)
    c: Coincident(g75,g72)
    c: Equal(g74,g73)
    c: Symmetric(g71,g72,g74)
    c: Coincident(g76,g74)
    c: Perpendicular(g45,g76)
    c: Coincident(g76,g61)
    c: Tangent(g62,g45) = 1.5708
    c: Tangent(g77,g36) = -1.5708
    c: Tangent(g77,g33) = -1.5708
    c: Tangent(g78,g35) = 1.5708
    c: Tangent(g78,g64) = 1.5708
    c: Radius(g78) = 1
    c: Radius(g77) = 1
    c: Coincident(g79,g34)
    c: PointOnObject(g79,g33)
    c: Horizontal(g79)
    c: Distance(g79) = 2
    c: Coincident(g80,g63)
    c: PointOnObject(g80,g28)
    c: Horizontal(g80)
    c: Parallel(g35,g29)
    c: Distance(g80) = 2
    c: Coincident(g81,g7)
    c: Tangent(g81,g27) = 1.5708
    c: Tangent(g81,g22) = -1.5708
    c: Radius(g81) = 1
    c: Coincident(g82,g7)
    c: Coincident(g82,g27)
    c: Perpendicular(g82,g27)
    c: Perpendicular(g7,g82)
FEATURE [Sketcher::SketchObject] Sketch003  label="right"
  FullyConstrained = true
  sketch-geometry (60):
    g0: LineSegment StartX=9 StartY=-25.5 StartZ=0 EndX=-9 EndY=-25.5 EndZ=0
    g1: GeomPoint X=19.8279 Y=-5 Z=0
    g2: LineSegment StartX=26.5712 StartY=-31.1874 StartZ=0 EndX=8.63967 EndY=-29.6186 EndZ=0
    g3: LineSegment StartX=31.0161 StartY=19.6186 StartZ=0 EndX=13.0846 EndY=21.1874 EndZ=0
    g4: GeomPoint X=38.2116 Y=-17 Z=0
    g5: LineSegment StartX=60.3734 StartY=-46.8011 StartZ=0 EndX=24.9203 EndY=-40.5498 EndZ=0
    g6: LineSegment StartX=36.7284 StartY=26.4172 StartZ=0 EndX=72.1815 EndY=20.1658 EndZ=0
    g7: LineSegment StartX=13.0846 StartY=21.1874 StartZ=0 EndX=8.63967 EndY=-29.6186 EndZ=0
    g8: LineSegment StartX=26.5712 StartY=-31.1874 StartZ=0 EndX=31.0161 EndY=19.6186 EndZ=0
    g9: LineSegment StartX=36.7284 StartY=26.4172 StartZ=0 EndX=24.9203 EndY=-40.5498 EndZ=0
    g10: LineSegment StartX=72.1815 StartY=20.1658 StartZ=0 EndX=60.3734 EndY=-46.8011 EndZ=0
    g11: GeomPoint X=45.5989 Y=-26.9337 Z=0
    g12: GeomPoint X=30.8244 Y=-7.0663 Z=0
    g13: LineSegment StartX=72.3551 StartY=21.1506 StartZ=0 EndX=36.9021 EndY=27.402 EndZ=0
    g14: LineSegment StartX=9 StartY=-25.5 StartZ=0 EndX=9 EndY=25.5 EndZ=0
    g15: GeomPoint X=73.1663 Y=19.9922 Z=0
    g16: ArcOfCircle CenterX=72.1815 CenterY=20.1658 CenterZ=0 NormalX=0 NormalY=0 NormalZ=1 AngleXU=0 Radius=1 StartAngle=6.10865 EndAngle=7.67945
    g17: LineSegment StartX=72.1815 StartY=20.1658 StartZ=0 EndX=125.976 EndY=15.4594 EndZ=0
    g18: LineSegment StartX=72.1815 StartY=20.1658 StartZ=0 EndX=75.1359 EndY=19.6449 EndZ=0
    g19: LineSegment StartX=72.1815 StartY=20.1658 StartZ=0 EndX=72.3551 EndY=21.1506 EndZ=0
    g20: LineSegment StartX=73.1663 StartY=19.9922 StartZ=0 EndX=70.2143 EndY=3.25045 EndZ=0
    g21: LineSegment StartX=70.2143 StartY=3.25045 StartZ=0 EndX=67.2623 EndY=-13.4913 EndZ=0
    g22: LineSegment StartX=67.2623 StartY=-13.4913 StartZ=0 EndX=64.3102 EndY=-30.233 EndZ=0
    g23: LineSegment StartX=64.3102 StartY=-30.233 StartZ=0 EndX=61.3582 EndY=-46.9747 EndZ=0
    g24: LineSegment StartX=76.2686 StartY=20.8121 StartZ=0 EndX=126.063 EndY=16.4556 EndZ=0
    g25: LineSegment StartX=125.976 StartY=15.4594 StartZ=0 EndX=120.049 EndY=-52.2818 EndZ=0
    g26: LineSegment StartX=75.1359 StartY=19.6449 StartZ=0 EndX=75.1967 EndY=19.9895 EndZ=0
    g27: ArcOfCircle CenterX=76.1815 CenterY=19.8159 CenterZ=0 NormalX=0 NormalY=0 NormalZ=1 AngleXU=0 Radius=1 StartAngle=1.48353 EndAngle=2.96706
    g28: ArcOfCircle CenterX=64.3331 CenterY=-47.3797 CenterZ=0 NormalX=0 NormalY=0 NormalZ=1 AngleXU=0 Radius=1 StartAngle=2.96706 EndAngle=4.59671
    g29: LineSegment StartX=119.962 StartY=-53.278 StartZ=0 EndX=66.1677 EndY=-48.5716 EndZ=0
    g30: LineSegment StartX=121.046 StartY=-52.369 StartZ=0 EndX=126.972 EndY=15.3723 EndZ=0
    g31: ArcOfCircle CenterX=73.934 CenterY=18.5875 CenterZ=0 NormalX=0 NormalY=0 NormalZ=1 AngleXU=0 Radius=1 StartAngle=2.96705 EndAngle=6.10865
    g32: ArcOfCircle CenterX=72.2844 CenterY=9.23185 CenterZ=0 NormalX=0 NormalY=0 NormalZ=1 AngleXU=0 Radius=1 StartAngle=6.10865 EndAngle=9.25025
    g33: LineSegment StartX=75.1359 StartY=19.6449 StartZ=0 EndX=74.9189 EndY=18.4139 EndZ=0
    g34: LineSegment StartX=70.2143 StartY=3.25045 StartZ=0 EndX=72.1839 EndY=2.90315 EndZ=0
    g35: LineSegment StartX=72.1839 StartY=2.90315 StartZ=0 EndX=73.2692 EndY=9.0582 EndZ=0
    g36: LineSegment StartX=72.1839 StartY=2.90315 StartZ=0 EndX=71.88 EndY=1.17974 EndZ=0
    g37: ArcOfCircle CenterX=70.8952 CenterY=1.35339 CenterZ=0 NormalX=0 NormalY=0 NormalZ=1 AngleXU=0 Radius=1 StartAngle=2.96706 EndAngle=6.10865
    g38: LineSegment StartX=67.2623 StartY=-13.4913 StartZ=0 EndX=69.2319 EndY=-13.8386 EndZ=0
    g39: LineSegment StartX=69.2319 StartY=-13.8386 StartZ=0 EndX=70.6645 EndY=-5.71392 EndZ=0
    g40: ArcOfCircle CenterX=69.6797 CenterY=-5.54027 CenterZ=0 NormalX=0 NormalY=0 NormalZ=1 AngleXU=0 Radius=1 StartAngle=6.10865 EndAngle=9.25025
    g41: LineSegment StartX=69.2319 StartY=-13.8386 StartZ=0 EndX=68.928 EndY=-15.562 EndZ=0
    g42: ArcOfCircle CenterX=67.9432 CenterY=-15.3883 CenterZ=0 NormalX=0 NormalY=0 NormalZ=1 AngleXU=0 Radius=1 StartAngle=2.96706 EndAngle=6.10865
    g43: LineSegment StartX=64.3102 StartY=-30.233 StartZ=0 EndX=66.2799 EndY=-30.5803 EndZ=0
    g44: LineSegment StartX=66.2799 StartY=-30.5803 StartZ=0 EndX=67.7125 EndY=-22.4556 EndZ=0
    g45: ArcOfCircle CenterX=66.7276 CenterY=-22.282 CenterZ=0 NormalX=0 NormalY=0 NormalZ=1 AngleXU=0 Radius=1 StartAngle=6.10865 EndAngle=9.25025
    g46: LineSegment StartX=66.2799 StartY=-30.5803 StartZ=0 EndX=65.3248 EndY=-35.9968 EndZ=0
    g47: ArcOfCircle CenterX=64.34 CenterY=-35.8231 CenterZ=0 NormalX=0 NormalY=0 NormalZ=1 AngleXU=0 Radius=1 StartAngle=2.96706 EndAngle=6.10865
    g48: LineSegment StartX=63.3483 StartY=-47.2061 StartZ=0 EndX=64.2829 EndY=-41.9056 EndZ=0
    g49: ArcOfCircle CenterX=63.2981 CenterY=-41.732 CenterZ=0 NormalX=0 NormalY=0 NormalZ=1 AngleXU=0 Radius=1 StartAngle=6.10865 EndAngle=9.25025
    g50: ArcOfCircle CenterX=72.1815 CenterY=20.1658 CenterZ=0 NormalX=0 NormalY=0 NormalZ=1 AngleXU=0 Radius=69 StartAngle=4.53786 EndAngle=4.62512
    g51: LineSegment StartX=64.34 StartY=-35.8231 StartZ=0 EndX=63.2981 EndY=-41.732 EndZ=0
    g52: LineSegment StartX=67.9432 StartY=-15.3883 StartZ=0 EndX=66.7276 EndY=-22.282 EndZ=0
    g53: LineSegment StartX=70.8952 StartY=1.35339 StartZ=0 EndX=69.6797 EndY=-5.54027 EndZ=0
    g54: LineSegment StartX=76.2686 StartY=20.8121 StartZ=0 EndX=72.3556 EndY=21.1544 EndZ=0
    g55: ArcOfCircle CenterX=60.3734 CenterY=-46.8011 CenterZ=0 NormalX=0 NormalY=0 NormalZ=1 AngleXU=0 Radius=1 StartAngle=4.53786 EndAngle=6.10865
    g56: ArcOfCircle CenterX=72.4428 CenterY=22.1506 CenterZ=0 NormalX=0 NormalY=0 NormalZ=1 AngleXU=0 Radius=1 StartAngle=4.53786 EndAngle=4.62512
    g57: LineSegment StartX=36.9021 StartY=27.402 StartZ=0 EndX=36.7284 EndY=26.4172 EndZ=0
    g58: ArcOfCircle CenterX=120.049 CenterY=-52.2818 CenterZ=0 NormalX=0 NormalY=0 NormalZ=1 AngleXU=0 Radius=1 StartAngle=4.62512 EndAngle=6.19592
    g59: ArcOfCircle CenterX=125.976 CenterY=15.4594 CenterZ=0 NormalX=0 NormalY=0 NormalZ=1 AngleXU=0 Radius=1 StartAngle=6.19592 EndAngle=7.76672
  constraints (153):
    c: Horizontal(g0)
    c: DistanceY(g-1,g1) = -5
    c: DistanceY(g4,g1) = 12
    c: Coincident(g7,g3)
    c: Coincident(g7,g2)
    c: Coincident(g8,g2)
    c: Coincident(g8,g3)
    c: PointOnObject(g0,g7)
    c: Perpendicular(g7,g3)
    c: Perpendicular(g8,g3)
    c: Perpendicular(g8,g2)
    c: Symmetric(g3,g2,g1)
    c: Distance(g2) = 18
    c: Coincident(g9,g6)
    c: Coincident(g9,g5)
    c: Perpendicular(g5,g9)
    c: Coincident(g10,g5)
    c: Distance(g5) = 36
    c: Distance(g9) = 68
    c: Perpendicular(g10,g6)
    c: Perpendicular(g5,g10)
    c: Symmetric(g5,g6,g12)
    c: Symmetric(g11,g12,g4)
    c: PointOnObject(g2,g9)
    c: Angle(g9,g8) = 0.0872665
    c: Perpendicular(g13,g9)
    c: Coincident(g14,g0)
    c: Vertical(g14)
    c: Symmetric(g14,g0,g-1)
    c: Distance(g14) = 51
    c: Distance(g0) = 18
    c: Angle(g7,g14) = 0.0872665
    c: Distance(g7) = 51
    c: Coincident(g6,g10)
    c: Symmetric(g12,g5,g11)
    c: Coincident(g16,g6)
    c: Coincident(g16,g13)
    c: Coincident(g16,g15)
    c: Coincident(g17,g6)
    c: Angle(g10,g17) = 1.65806
    c: Distance(g17) = 54
    c: Coincident(g18,g6)
    c: Perpendicular(g10,g18)
    c: Distance(g18) = 3
    c: PointOnObject(g16,g18)
    c: Coincident(g19,g6)
    c: Coincident(g19,g13)
    c: Perpendicular(g6,g19)
    c: Coincident(g20,g16)
    c: Coincident(g21,g20)
    c: Distance(g20) = 17
    c: Distance(g21) = 17
    c: Perpendicular(g20,g18)
    c: Parallel(g20,g21)
    c: Coincident(g22,g21)
    c: Distance(g22) = 17
    c: Parallel(g21,g22)
    c: Coincident(g23,g22)
    c: Distance(g23) = 17
    c: Parallel(g23,g22)
    c: Coincident(g25,g17)
    c: Perpendicular(g25,g17)
    c: Distance(g25) = 68
    c: Coincident(g26,g18)
    c: Radius(g27) = 1
    c: Perpendicular(g18,g26)
    c: Tangent(g27,g24) = 1.5708
    c: Tangent(g27,g26) = 1.5708
    c: Parallel(g24,g17)
    c: Radius(g28) = 1
    c: Perpendicular(g25,g29)
    c: PointOnObject(g31,g20)
    c: Radius(g31) = 1
    c: Radius(g32) = 1
    c: Coincident(g33,g18)
    c: Coincident(g33,g31)
    c: Tangent(g33,g31)
    c: Perpendicular(g33,g18)
    c: Distance(g33) = 1.25
    c: Coincident(g34,g20)
    c: Distance(g34) = 2
    c: Perpendicular(g34,g20)
    c: Coincident(g35,g34)
    c: Distance(g35) = 6.25
    c: Tangent(g35,g32) = -1.5708
    c: Coincident(g36,g34)
    c: Perpendicular(g36,g34)
    c: Distance(g36) = 1.75
    c: Tangent(g37,g36) = 1.5708
    c: Tangent(g37,g21) = -1.5708
    c: Coincident(g38,g21)
    c: Distance(g38) = 2
    c: Perpendicular(g38,g21)
    c: Coincident(g39,g38)
    c: Perpendicular(g38,g39)
    c: Coincident(g40,g39)
    c: Radius(g40) = 1
    c: Tangent(g40,g21) = -1.5708
    c: Coincident(g41,g38)
    c: Perpendicular(g41,g38)
    c: Tangent(g42,g41) = 1.5708
    c: Tangent(g42,g22) = -1.5708
    c: Coincident(g43,g22)
    c: Perpendicular(g23,g43)
    c: Distance(g43) = 2
    c: Coincident(g44,g43)
    c: Perpendicular(g43,g44)
    c: Tangent(g45,g22) = -1.5708
    c: Coincident(g46,g43)
    c: Perpendicular(g46,g43)
    c: Coincident(g47,g46)
    c: Tangent(g47,g23) = -1.5708
    c: Radius(g47) = 1
    c: Tangent(g49,g23) = -1.5708
    c: Radius(g49) = 1
    c: Coincident(g50,g6)
    c: Tangent(g50,g29) = 1.5708
    c: Tangent(g28,g50) = -1.5708
    c: Tangent(g45,g44) = -1.5708
    c: Tangent(g48,g28) = 1.5708
    c: Tangent(g49,g48) = -1.5708
    c: Parallel(g48,g23)
    c: Coincident(g51,g47)
    c: Coincident(g51,g49)
    c: Distance(g51) = 6
    c: Distance(g41) = 1.75
    c: Coincident(g52,g42)
    c: Coincident(g52,g45)
    c: Distance(g52) = 7
    c: Coincident(g53,g37)
    c: Coincident(g53,g40)
    c: Distance(g53) = 7
    c: Coincident(g54,g24)
    c: Parallel(g54,g24)
    c: Distance(g46) = 5.5
    c: Coincident(g55,g5)
    c: Coincident(g55,g23)
    c: Tangent(g56,g13) = 1.5708
    c: Tangent(g56,g54) = 1.5708
    c: Radius(g56) = 1
    c: Coincident(g57,g13)
    c: Coincident(g57,g6)
    c: Perpendicular(g57,g6)
    c: Tangent(g55,g50) = -1.5708
    c: Tangent(g32,g20) = -1.5708
    c: Coincident(g58,g25)
    c: Coincident(g59,g17)
    c: Tangent(g59,g24) = 1.5708
    c: Tangent(g59,g30) = -1.5708
    c: Tangent(g58,g30) = -1.5708
    c: Tangent(g58,g29) = 1.5708
    c: Parallel(g30,g25)
    c: Radius(g59) = 1
FEATURE [Sketcher::SketchObject] Sketch005  label="outer"
  FullyConstrained = true
  sketch-geometry (65):
    g0: GeomPoint X=-19.8279 Y=-5 Z=0
    g1: LineSegment StartX=9 StartY=-25.5 StartZ=0 EndX=-9 EndY=-25.5 EndZ=0
    g2: LineSegment StartX=9 StartY=42.5 StartZ=0 EndX=-9 EndY=42.5 EndZ=0
    g3: LineSegment StartX=-13.0846 StartY=21.1874 StartZ=0 EndX=-31.0161 EndY=19.6186 EndZ=0
    g4: LineSegment StartX=-13.0846 StartY=21.1874 StartZ=0 EndX=-14.5663 EndY=38.1227 EndZ=0
    g5: GeomPoint X=19.8279 Y=-5 Z=0
    g6: LineSegment StartX=26.5712 StartY=-31.1874 StartZ=0 EndX=8.63967 EndY=-29.6186 EndZ=0
    g7: LineSegment StartX=31.0161 StartY=19.6186 StartZ=0 EndX=13.0846 EndY=21.1874 EndZ=0
    g8: LineSegment StartX=32.4978 StartY=36.5539 StartZ=0 EndX=14.5663 EndY=38.1227 EndZ=0
    g9: LineSegment StartX=-31.0161 StartY=19.6186 StartZ=0 EndX=-48.9476 EndY=18.0498 EndZ=0
    g10: GeomPoint X=38.2116 Y=-17 Z=0
    g11: LineSegment StartX=60.3734 StartY=-46.8011 StartZ=0 EndX=24.9203 EndY=-40.5498 EndZ=0
    g12: LineSegment StartX=36.7284 StartY=26.4172 StartZ=0 EndX=72.1815 EndY=20.1658 EndZ=0
    g13: LineSegment StartX=13.0846 StartY=21.1874 StartZ=0 EndX=8.63967 EndY=-29.6186 EndZ=0
    g14: LineSegment StartX=26.5712 StartY=-31.1874 StartZ=0 EndX=31.0161 EndY=19.6186 EndZ=0
    g15: LineSegment StartX=-13.0846 StartY=21.1874 StartZ=0 EndX=-8.63967 EndY=-29.6186 EndZ=0
    g16: LineSegment StartX=-48.9476 StartY=18.0498 StartZ=0 EndX=-44.5027 EndY=-32.7562 EndZ=0
    g17: LineSegment StartX=-14.5663 StartY=38.1227 StartZ=0 EndX=-50.4293 EndY=34.9851 EndZ=0
    g18: LineSegment StartX=-8.63967 StartY=-29.6186 StartZ=0 EndX=-44.5027 EndY=-32.7562 EndZ=0
    g19: GeomPoint X=-28.7936 Y=-5.7844 Z=0
    g20: GeomPoint X=-10.8621 Y=-4.2156 Z=0
    g21: LineSegment StartX=36.7284 StartY=26.4172 StartZ=0 EndX=24.9203 EndY=-40.5498 EndZ=0
    g22: LineSegment StartX=72.1815 StartY=20.1658 StartZ=0 EndX=60.3734 EndY=-46.8011 EndZ=0
    g23: GeomPoint X=45.5989 Y=-26.9337 Z=0
    g24: GeomPoint X=30.8244 Y=-7.0663 Z=0
    g25: LineSegment StartX=33.494 StartY=36.4667 StartZ=0 EndX=32.3471 EndY=23.3585 EndZ=0
    g26: LineSegment StartX=9 StartY=43.5 StartZ=0 EndX=-9 EndY=43.5 EndZ=0
    g27: LineSegment StartX=31.0161 StartY=19.6186 StartZ=0 EndX=32.4978 EndY=36.5539 EndZ=0
    g28: LineSegment StartX=-50.1181 StartY=19.955 StartZ=0 EndX=-51.4255 EndY=34.8979 EndZ=0
    g29: LineSegment StartX=-48.9476 StartY=18.0498 StartZ=0 EndX=-49.2962 EndY=22.0345 EndZ=0
    g30: LineSegment StartX=-49.2962 StartY=22.0345 StartZ=0 EndX=-50.4293 EndY=34.9851 EndZ=0
    g31: LineSegment StartX=14.5663 StartY=38.1227 StartZ=0 EndX=13.0846 EndY=21.1874 EndZ=0
    g32: GeomPoint X=-32.4978 Y=36.5539 Z=0
    g33: GeomPoint X=23.532 Y=37.3383 Z=0
    g34: LineSegment StartX=-50.5164 StartY=35.9813 StartZ=0 EndX=-23.6192 EndY=38.3345 EndZ=0
    g35: LineSegment StartX=23.6192 StartY=38.3345 StartZ=0 EndX=32.5849 EndY=37.5501 EndZ=0
    g36: ArcOfCircle CenterX=7.14e-14 CenterY=-231.634 CenterZ=0 NormalX=0 NormalY=0 NormalZ=1 AngleXU=0 Radius=271 StartAngle=1.48353 EndAngle=1.65806
    g37: GeomPoint X=-23.532 Y=37.3383 Z=0
    g38: LineSegment StartX=-23.6192 StartY=38.3345 StartZ=0 EndX=-23.532 EndY=37.3383 EndZ=0
    g39: GeomPoint X=23.532 Y=37.3383 Z=0
    g40: LineSegment StartX=23.6192 StartY=38.3345 StartZ=0 EndX=23.532 EndY=37.3383 EndZ=0
    g41: ArcOfCircle CenterX=-51.1143 CenterY=19.8678 CenterZ=0 NormalX=0 NormalY=0 NormalZ=1 AngleXU=0 Radius=1 StartAngle=4.79966 EndAngle=6.37045
    g42: LineSegment StartX=-22.0504 StartY=20.403 StartZ=0 EndX=-22.3118 EndY=23.3915 EndZ=0
    g43: LineSegment StartX=22.0504 StartY=20.403 StartZ=0 EndX=22.3118 EndY=23.3915 EndZ=0
    g44: ArcOfCircle CenterX=-1.742e-13 CenterY=-231.634 CenterZ=0 NormalX=0 NormalY=0 NormalZ=1 AngleXU=0 Radius=256 StartAngle=1.44837 EndAngle=1.65806
    g45: ArcOfCircle CenterX=31.351 CenterY=23.4457 CenterZ=0 NormalX=0 NormalY=0 NormalZ=1 AngleXU=0 Radius=1 StartAngle=4.62512 EndAngle=6.19592
    g46: LineSegment StartX=36.7284 StartY=26.4172 StartZ=0 EndX=36.9021 EndY=27.402 EndZ=0
    g47: ArcOfCircle CenterX=33.8408 CenterY=28.9572 CenterZ=0 NormalX=0 NormalY=0 NormalZ=1 AngleXU=0 Radius=1 StartAngle=3.05433 EndAngle=4.53786
    g48: LineSegment StartX=36.9021 StartY=27.402 StartZ=0 EndX=33.6671 EndY=27.9724 EndZ=0
    g49: ArcOfCircle CenterX=-9 CenterY=42.5 CenterZ=0 NormalX=0 NormalY=0 NormalZ=1 AngleXU=0 Radius=1 StartAngle=1.5708 EndAngle=3.14159
    g50: ArcOfCircle CenterX=-11 CenterY=40.1432 CenterZ=0 NormalX=0 NormalY=0 NormalZ=1 AngleXU=0 Radius=1 StartAngle=4.75284 EndAngle=6.28319
    g51: ArcOfCircle CenterX=10.74 CenterY=39.8934 CenterZ=0 NormalX=0 NormalY=0 NormalZ=1 AngleXU=0 Radius=0.74 StartAngle=3.14159 EndAngle=4.67286
    g52: ArcOfCircle CenterX=9 CenterY=42.5 CenterZ=0 NormalX=0 NormalY=0 NormalZ=1 AngleXU=0 Radius=1 StartAngle=1e-16 EndAngle=1.5708
    g53: LineSegment StartX=-10 StartY=40.1432 StartZ=0 EndX=-10 EndY=42.5 EndZ=0
    g54: LineSegment StartX=10 StartY=42.5 StartZ=0 EndX=10 EndY=39.8934 EndZ=0
    g55: LineSegment StartX=-9 StartY=-25.5 StartZ=0 EndX=-9 EndY=42.5 EndZ=0
    g56: LineSegment StartX=9 StartY=42.5 StartZ=0 EndX=9 EndY=-25.5 EndZ=0
    g57: GeomPoint X=3e-16 Y=8.5 Z=0
    g58: GeomPoint X=-4.5 Y=-8.5 Z=0
    g59: GeomPoint X=4.5 Y=-8.5 Z=0
    g60: GeomPoint X=-3e-16 Y=-8.5 Z=0
    g61: ArcOfCircle CenterX=32.4978 CenterY=36.5539 CenterZ=0 NormalX=0 NormalY=0 NormalZ=1 AngleXU=0 Radius=1 StartAngle=6.19592 EndAngle=7.76672
    g62: ArcOfCircle CenterX=-50.4293 CenterY=34.9851 CenterZ=0 NormalX=0 NormalY=0 NormalZ=1 AngleXU=0 Radius=1 StartAngle=1.65806 EndAngle=3.22886
    g63: ArcOfCircle CenterX=-49.2962 CenterY=22.0345 CenterZ=0 NormalX=0 NormalY=0 NormalZ=1 AngleXU=0 Radius=1 StartAngle=3.22886 EndAngle=4.79966
    g64: LineSegment StartX=-51.0272 StartY=18.8716 StartZ=0 EndX=-49.0348 EndY=19.046 EndZ=0
  constraints (149):
    c: DistanceY(g0,g-1) = 5
    c: Horizontal(g1)
    c: Horizontal(g2)
    c: DistanceX(g2,g2) = 18
    c: Perpendicular(g3,g4)
    c: Distance(g4) = 17
    c: DistanceY(g-1,g5) = -5
    c: Coincident(g9,g3)
    c: DistanceY(g10,g5) = 12
    c: Coincident(g13,g7)
    c: Coincident(g13,g6)
    c: Coincident(g14,g6)
    c: Coincident(g14,g7)
    c: PointOnObject(g1,g13)
    c: Coincident(g15,g3)
    c: PointOnObject(g1,g15)
    c: Coincident(g16,g9)
    c: Symmetric(g3,g15,g0)
    c: Coincident(g17,g4)
    c: Coincident(g3,g4)
    c: Perpendicular(g3,g15)
    c: Perpendicular(g16,g9)
    c: Perpendicular(g4,g17)
    c: Coincident(g18,g15)
    c: Coincident(g18,g16)
    c: Symmetric(g9,g15,g19)
    c: Symmetric(g3,g15,g20)
    c: Symmetric(g20,g19,g0)
    c: Distance(g18) = 36
    c: Perpendicular(g16,g18)
    c: Perpendicular(g13,g7)
    c: Perpendicular(g14,g7)
    c: Perpendicular(g14,g6)
    c: Symmetric(g7,g6,g5)
    c: Distance(g6) = 18
    c: Coincident(g21,g12)
    c: Coincident(g21,g11)
    c: Perpendicular(g11,g21)
    c: Coincident(g22,g11)
    c: Distance(g11) = 36
    c: Distance(g21) = 68
    c: Perpendicular(g22,g12)
    c: Perpendicular(g11,g22)
    c: Symmetric(g11,g12,g24)
    c: Symmetric(g23,g24,g10)
    c: PointOnObject(g6,g21)
    c: Angle(g21,g14) = 0.0872665
    c: Coincident(g27,g8)
    c: Perpendicular(g8,g27)
    c: Coincident(g29,g9)
    c: Coincident(g30,g17)
    c: Perpendicular(g9,g29)
    c: Perpendicular(g30,g17)
    c: Coincident(g22,g12)
    c: Symmetric(g24,g11,g23)
    c: Coincident(g31,g8)
    c: Coincident(g31,g7)
    c: Distance(g31) = 17
    c: Perpendicular(g8,g31)
    c: Parallel(g25,g27)
    c: Coincident(g29,g30)
    c: Distance(g29) = 4
    c: Symmetric(g17,g4,g32)
    c: Symmetric(g8,g8,g33)
    c: Parallel(g34,g17)
    c: Tangent(g34,g36) = 1.5708
    c: Symmetric(g32,g4,g37)
    c: Coincident(g38,g34)
    c: Coincident(g38,g37)
    c: Perpendicular(g38,g17)
    c: Parallel(g35,g8)
    c: Coincident(g35,g36)
    c: Coincident(g40,g35)
    c: Coincident(g40,g39)
    c: Perpendicular(g40,g8)
    c: Coincident(g40,g33)
    c: Perpendicular(g7,g31)
    c: Coincident(g27,g7)
    c: Perpendicular(g7,g43)
    c: Distance(g43) = 3
    c: Symmetric(g7,g7,g43)
    c: Symmetric(g3,g3,g42)
    c: Perpendicular(g3,g42)
    c: Distance(g42) = 3
    c: Coincident(g44,g42)
    c: Perpendicular(g44,g42)
    c: PointOnObject(g43,g44)
    c: PointOnObject(g44,g27)
    c: PointOnObject(g45,g27)
    c: Coincident(g45,g44)
    c: Tangent(g25,g45) = 1.5708
    c: Coincident(g46,g12)
    c: Perpendicular(g12,g46)
    c: Distance(g46) = 1
    c: Tangent(g47,g25) = -1.5708
    c: Radius(g47) = 1
    c: Coincident(g48,g46)
    c: Perpendicular(g46,g48)
    c: Tangent(g48,g47) = 1.5708
    c: Coincident(g49,g2)
    c: Coincident(g52,g2)
    c: Tangent(g49,g26) = -1.5708
    c: Tangent(g53,g49) = 1.5708
    c: Tangent(g53,g50) = -1.5708
    c: Tangent(g50,g36) = 1.5708
    c: Tangent(g51,g36) = 1.5708
    c: Tangent(g54,g51) = -1.5708
    c: Tangent(g54,g52) = 1.5708
    c: Tangent(g52,g26) = -1.5708
    c: Horizontal(g26)
    c: Vertical(g53)
    c: Vertical(g54)
    c: Radius(g52) = 1
    c: Radius(g50) = 1
    c: Radius(g51) = 0.74
    c: Coincident(g55,g1)
    c: Coincident(g55,g2)
    c: Vertical(g55)
    c: Coincident(g56,g2)
    c: Coincident(g56,g1)
    c: Vertical(g56)
    c: Distance(g55) = 68
    c: Angle(g55,g15) = 0.0872665
    c: Angle(g13,g56) = 0.0872665
    c: Symmetric(g2,g1,g57)
    c: Symmetric(g1,g57,g58)
    c: Symmetric(g57,g1,g59)
    c: Symmetric(g59,g58,g60)
    c: Symmetric(g57,g60,g-1)
    c: Distance(g15) = 51
    c: Distance(g13) = 51
    c: Coincident(g61,g8)
    c: Tangent(g61,g35) = 1.5708
    c: Tangent(g61,g25) = 1.5708
    c: Radius(g61) = 1
    c: Coincident(g62,g17)
    c: Tangent(g62,g34) = 1.5708
    c: Tangent(g62,g28) = 1.5708
    c: Radius(g62) = 1
    c: Coincident(g63,g29)
    c: PointOnObject(g63,g29)
    c: Tangent(g63,g28) = 1.5708
    c: Radius(g41) = 1
    c: Radius(g63) = 1
    c: PointOnObject(g64,g29)
    c: Tangent(g64,g41) = -1.5708
    c: Tangent(g41,g28) = -1.5708
    c: Perpendicular(g29,g64)
    c: Distance(g64,g9) = 1
FEATURE [Sketcher::SketchObject] Sketch004  label="side"
  FullyConstrained = true
  sketch-geometry (56):
    g0: GeomPoint X=-19.8279 Y=-5 Z=0
    g1: LineSegment StartX=9 StartY=-25.5 StartZ=0 EndX=-9 EndY=-25.5 EndZ=0
    g2: LineSegment StartX=-13.0846 StartY=21.1874 StartZ=0 EndX=-31.0161 EndY=19.6186 EndZ=0
    g3: GeomPoint X=19.8279 Y=-5 Z=0
    g4: LineSegment StartX=26.5712 StartY=-31.1874 StartZ=0 EndX=8.63967 EndY=-29.6186 EndZ=0
    g5: LineSegment StartX=31.0161 StartY=19.6186 StartZ=0 EndX=13.0846 EndY=21.1874 EndZ=0
    g6: LineSegment StartX=-31.0161 StartY=19.6186 StartZ=0 EndX=-48.9476 EndY=18.0498 EndZ=0
    g7: GeomPoint X=38.2116 Y=-17 Z=0
    g8: LineSegment StartX=60.3734 StartY=-46.8011 StartZ=0 EndX=24.9203 EndY=-40.5498 EndZ=0
    g9: LineSegment StartX=-20.4485 StartY=-30.846 StartZ=0 EndX=-37.8352 EndY=-35.5048 EndZ=0
    g10: LineSegment StartX=-37.8352 StartY=-35.5048 StartZ=0 EndX=-33.4353 EndY=-51.9255 EndZ=0
    g11: LineSegment StartX=-33.4353 StartY=-51.9255 StartZ=0 EndX=-16.0486 EndY=-47.2668 EndZ=0
    g12: LineSegment StartX=-16.0486 StartY=-47.2668 StartZ=0 EndX=-20.4485 EndY=-30.846 EndZ=0
    g13: LineSegment StartX=-50.4353 StartY=-22.4806 StartZ=0 EndX=-66.0237 EndY=-31.4806 EndZ=0
    g14: LineSegment StartX=-66.0237 StartY=-31.4806 StartZ=0 EndX=-49.0237 EndY=-60.9255 EndZ=0
    g15: LineSegment StartX=-49.0237 StartY=-60.9255 StartZ=0 EndX=-33.4353 EndY=-51.9255 EndZ=0
    g16: LineSegment StartX=-33.4353 StartY=-51.9255 StartZ=0 EndX=-50.4353 EndY=-22.4806 EndZ=0
    g17: LineSegment StartX=-16.0486 StartY=-30.2668 StartZ=0 EndX=1.9514 EndY=-30.2668 EndZ=0
    g18: LineSegment StartX=-16.0486 StartY=-47.2668 StartZ=0 EndX=-16.0486 EndY=-30.2668 EndZ=0
    g19: LineSegment StartX=1.9514 StartY=-47.2668 StartZ=0 EndX=-16.0486 EndY=-47.2668 EndZ=0
    g20: LineSegment StartX=36.7284 StartY=26.4172 StartZ=0 EndX=72.1815 EndY=20.1658 EndZ=0
    g21: LineSegment StartX=13.0846 StartY=21.1874 StartZ=0 EndX=8.63967 EndY=-29.6186 EndZ=0
    g22: LineSegment StartX=26.5712 StartY=-31.1874 StartZ=0 EndX=31.0161 EndY=19.6186 EndZ=0
    g23: LineSegment StartX=-13.0846 StartY=21.1874 StartZ=0 EndX=-8.63967 EndY=-29.6186 EndZ=0
    g24: LineSegment StartX=-48.9476 StartY=18.0498 StartZ=0 EndX=-44.5027 EndY=-32.7562 EndZ=0
    g25: LineSegment StartX=-8.63967 StartY=-29.6186 StartZ=0 EndX=-44.5027 EndY=-32.7562 EndZ=0
    g26: GeomPoint X=-28.7936 Y=-5.7844 Z=0
    g27: GeomPoint X=-10.8621 Y=-4.2156 Z=0
    g28: LineSegment StartX=-9 StartY=25.5 StartZ=0 EndX=-9 EndY=-25.5 EndZ=0
    g29: LineSegment StartX=36.7284 StartY=26.4172 StartZ=0 EndX=24.9203 EndY=-40.5498 EndZ=0
    g30: LineSegment StartX=72.1815 StartY=20.1658 StartZ=0 EndX=60.3734 EndY=-46.8011 EndZ=0
    g31: GeomPoint X=45.5989 Y=-26.9337 Z=0
    g32: GeomPoint X=30.8244 Y=-7.0663 Z=0
    g33: ArcOfCircle CenterX=-7.0486 CenterY=-115.629 CenterZ=0 NormalX=0 NormalY=0 NormalZ=1 AngleXU=0 Radius=67.3618 StartAngle=1.5708 EndAngle=2.0944
    g34: LineSegment StartX=-7.0486 StartY=-48.2668 StartZ=0 EndX=1.9514 EndY=-48.2668 EndZ=0
    g35: LineSegment StartX=2.9514 StartY=-31.6733 StartZ=0 EndX=2.9514 EndY=-47.2668 EndZ=0
    g36: LineSegment StartX=9 StartY=-25.5 StartZ=0 EndX=9 EndY=25.5 EndZ=0
    g37: LineSegment StartX=9 StartY=25.5 StartZ=0 EndX=-9 EndY=25.5 EndZ=0
    g38: LineSegment StartX=1.9514 StartY=-47.2668 StartZ=0 EndX=1.9514 EndY=-30.2668 EndZ=0
    g39: ArcOfCircle CenterX=-49.0237 CenterY=-60.9255 CenterZ=0 NormalX=0 NormalY=0 NormalZ=1 AngleXU=0 Radius=1 StartAngle=3.66519 EndAngle=5.23599
    g40: LineSegment StartX=-40.7295 StartY=-57.2915 StartZ=0 EndX=-48.5237 EndY=-61.7915 EndZ=0
    g41: LineSegment StartX=-66.8897 StartY=-31.9806 StartZ=0 EndX=-49.8897 EndY=-61.4255 EndZ=0
    g42: LineSegment StartX=-66.0237 StartY=-31.4806 StartZ=0 EndX=-66.8897 EndY=-31.9806 EndZ=0
    g43: LineSegment StartX=19.8279 StartY=-5 StartZ=0 EndX=0 EndY=-231.634 EndZ=0
    g44: ArcOfCircle CenterX=0 CenterY=-231.634 CenterZ=0 NormalX=0 NormalY=0 NormalZ=1 AngleXU=0 Radius=201 StartAngle=1.44949 EndAngle=1.55104
    g45: ArcOfCircle CenterX=3.9514 CenterY=-31.6733 CenterZ=0 NormalX=0 NormalY=0 NormalZ=1 AngleXU=0 Radius=1 StartAngle=1.55104 EndAngle=3.14159
    g46: LineSegment StartX=60.1998 StartY=-47.7859 StartZ=0 EndX=24.7467 EndY=-41.5346 EndZ=0
    g47: ArcOfCircle CenterX=24.9203 CenterY=-40.5498 CenterZ=0 NormalX=0 NormalY=0 NormalZ=1 AngleXU=0 Radius=1 StartAngle=2.96706 EndAngle=4.53786
    g48: ArcOfCircle CenterX=24.2024 CenterY=-33.1041 CenterZ=0 NormalX=0 NormalY=0 NormalZ=1 AngleXU=0 Radius=1 StartAngle=6.10865 EndAngle=7.73267
    g49: LineSegment StartX=25.1872 StartY=-33.2777 StartZ=0 EndX=23.9355 EndY=-40.3761 EndZ=0
    g50: GeomPoint X=-24.7419 Y=-49.5961 Z=0
    g51: LineSegment StartX=-24.7419 StartY=-49.5961 StartZ=0 EndX=-24.4831 EndY=-50.5621 EndZ=0
    g52: GeomPoint X=17.6054 Y=-30.403 Z=0
    g53: LineSegment StartX=17.6054 StartY=-30.403 StartZ=0 EndX=17.5183 EndY=-31.3992 EndZ=0
    g54: ArcOfCircle CenterX=1.9514 CenterY=-47.2668 CenterZ=0 NormalX=0 NormalY=0 NormalZ=1 AngleXU=0 Radius=1 StartAngle=4.71239 EndAngle=6.28319
    g55: LineSegment StartX=60.3734 StartY=-46.8011 StartZ=0 EndX=60.1998 EndY=-47.7859 EndZ=0
  constraints (138):
    c: DistanceY(g0,g-1) = 5
    c: Horizontal(g1)
    c: DistanceY(g-1,g3) = -5
    c: Coincident(g6,g2)
    c: DistanceY(g7,g3) = 12
    c: Coincident(g10,g9)
    c: Coincident(g12,g11)
    c: Coincident(g12,g9)
    c: Perpendicular(g9,g12)
    c: Perpendicular(g10,g9)
    c: Perpendicular(g10,g11)
    c: Distance(g9) = 18
    c: Distance(g12) = 17
    c: Coincident(g14,g13)
    c: Coincident(g15,g14)
    c: Coincident(g16,g15)
    c: Coincident(g16,g13)
    c: Perpendicular(g14,g13)
    c: Perpendicular(g16,g13)
    c: Perpendicular(g15,g16)
    c: Distance(g13) = 18
    c: Distance(g16) = 34
    c: Coincident(g18,g17)
    c: Horizontal(g17)
    c: Vertical(g18)
    c: Distance(g17) = 18
    c: Coincident(g10,g15)
    c: Angle(g18,g12) = 0.261799
    c: Angle(g16,g10) = -0.261799
    c: Coincident(g19,g11)
    c: Horizontal(g19)
    c: Coincident(g21,g5)
    c: Coincident(g21,g4)
    c: Coincident(g22,g4)
    c: Coincident(g22,g5)
    c: PointOnObject(g1,g21)
    c: Coincident(g23,g2)
    c: PointOnObject(g1,g23)
    c: Coincident(g24,g6)
    c: Symmetric(g2,g23,g0)
    c: Perpendicular(g2,g23)
    c: Perpendicular(g24,g6)
    c: Coincident(g25,g23)
    c: Coincident(g25,g24)
    c: Symmetric(g6,g23,g26)
    c: Symmetric(g2,g23,g27)
    c: Symmetric(g27,g26,g0)
    c: Distance(g25) = 36
    c: Perpendicular(g24,g25)
    c: Perpendicular(g21,g5)
    c: Perpendicular(g22,g5)
    c: Perpendicular(g22,g4)
    c: Symmetric(g5,g4,g3)
    c: Distance(g4) = 18
    c: Coincident(g28,g1)
    c: Vertical(g28)
    c: Symmetric(g28,g1,g-1)
    c: Distance(g28) = 51
    c: Equal(g28,g23)
    c: Angle(g28,g23) = 0.0872665
    c: Coincident(g29,g20)
    c: Coincident(g29,g8)
    c: Perpendicular(g8,g29)
    c: Coincident(g30,g8)
    c: Distance(g8) = 36
    c: Distance(g29) = 68
    c: Perpendicular(g30,g20)
    c: Perpendicular(g8,g30)
    c: Symmetric(g8,g20,g32)
    c: Symmetric(g31,g32,g7)
    c: PointOnObject(g4,g29)
    c: Angle(g29,g22) = 0.0872665
    c: Horizontal(g34)
    c: Coincident(g18,g11)
    c: Coincident(g30,g20)
    c: Symmetric(g32,g8,g31)
    c: Coincident(g36,g1)
    c: Vertical(g36)
    c: Coincident(g37,g36)
    c: Coincident(g37,g28)
    c: Horizontal(g37)
    c: Distance(g37) = 18
    c: Angle(g21,g36) = 0.0872665
    c: Distance(g21) = 51
    c: PointOnObject(g24,g16)
    c: Tangent(g33,g34) = 1.5708
    c: Coincident(g38,g19)
    c: Vertical(g38)
    c: Coincident(g17,g38)
    c: Distance(g38) = 17
    c: PointOnObject(g17,g25)
    c: Coincident(g39,g14)
    c: Radius(g39) = 1
    c: Coincident(g42,g13)
    c: Coincident(g42,g41)
    c: Perpendicular(g42,g14)
    c: Parallel(g41,g14)
    c: Parallel(g40,g15)
    c: Tangent(g41,g39) = -1.5708
    c: Vertical(g35)
    c: Coincident(g43,g3)
    c: PointOnObject(g43,g-2)
    c: Perpendicular(g4,g43)
    c: Coincident(g44,g43)
    c: Tangent(g45,g35) = -1.5708
    c: Tangent(g45,g44) = -1.5708
    c: Radius(g45) = 1
    c: Coincident(g47,g8)
    c: Tangent(g49,g47) = -1.5708
    c: Tangent(g49,g48) = 1.5708
    c: Radius(g48) = 1
    c: Parallel(g49,g29)
    c: Radius(g47) = 1
    c: Tangent(g47,g46) = 1.5708
    c: Tangent(g33,g40) = -1.5708
    c: Coincident(g11,g10)
    c: Tangent(g40,g39) = 1.5708
    c: Symmetric(g10,g11,g50)
    c: Coincident(g51,g50)
    c: PointOnObject(g51,g33)
    c: Perpendicular(g33,g51)
    c: Distance(g51) = 1
    c: PointOnObject(g52,g4)
    c: PointOnObject(g52,g43)
    c: Tangent(g44,g48) = -1.5708
    c: PointOnObject(g53,g4)
    c: PointOnObject(g53,g44)
    c: Perpendicular(g53,g4)
    c: Distance(g53) = 1
    c: Perpendicular(g44,g53)
    c: Coincident(g54,g19)
    c: Tangent(g54,g35) = 1.5708
    c: Tangent(g54,g34) = -1.5708
    c: Radius(g54) = 1
    c: Coincident(g55,g8)
    c: Coincident(g55,g46)
    c: Perpendicular(g46,g55)
    c: Perpendicular(g8,g55)
FEATURE [Sketcher::SketchObject] Sketch006  label="side_inner"
  FullyConstrained = true
  sketch-geometry (55):
    g0: GeomPoint X=-19.8279 Y=-5 Z=0
    g1: LineSegment StartX=9 StartY=-25.5 StartZ=0 EndX=-9 EndY=-25.5 EndZ=0
    g2: LineSegment StartX=-13.0846 StartY=21.1874 StartZ=0 EndX=-31.0161 EndY=19.6186 EndZ=0
    g3: LineSegment StartX=-31.0161 StartY=19.6186 StartZ=0 EndX=-48.9476 EndY=18.0498 EndZ=0
    g4: LineSegment StartX=-20.4485 StartY=-30.846 StartZ=0 EndX=-37.8352 EndY=-35.5048 EndZ=0
    g5: LineSegment StartX=-37.8352 StartY=-35.5048 StartZ=0 EndX=-33.4353 EndY=-51.9255 EndZ=0
    g6: LineSegment StartX=-33.4353 StartY=-51.9255 StartZ=0 EndX=-16.0486 EndY=-47.2668 EndZ=0
    g7: LineSegment StartX=-16.0486 StartY=-47.2668 StartZ=0 EndX=-20.4485 EndY=-30.846 EndZ=0
    g8: LineSegment StartX=-50.4353 StartY=-22.4806 StartZ=0 EndX=-66.0237 EndY=-31.4806 EndZ=0
    g9: LineSegment StartX=-66.0237 StartY=-31.4806 StartZ=0 EndX=-49.0237 EndY=-60.9255 EndZ=0
    g10: LineSegment StartX=-49.0237 StartY=-60.9255 StartZ=0 EndX=-33.4353 EndY=-51.9255 EndZ=0
    g11: LineSegment StartX=-33.4353 StartY=-51.9255 StartZ=0 EndX=-50.4353 EndY=-22.4806 EndZ=0
    g12: LineSegment StartX=-16.0486 StartY=-30.2668 StartZ=0 EndX=1.9514 EndY=-30.2668 EndZ=0
    g13: LineSegment StartX=1.9514 StartY=-30.2668 StartZ=0 EndX=1.9514 EndY=-47.2668 EndZ=0
    g14: LineSegment StartX=-16.0486 StartY=-47.2668 StartZ=0 EndX=-16.0486 EndY=-30.2668 EndZ=0
    g15: LineSegment StartX=1.9514 StartY=-47.2668 StartZ=0 EndX=-16.0486 EndY=-47.2668 EndZ=0
    g16: LineSegment StartX=-13.0846 StartY=21.1874 StartZ=0 EndX=-8.63967 EndY=-29.6186 EndZ=0
    g17: LineSegment StartX=-48.9476 StartY=18.0498 StartZ=0 EndX=-44.5027 EndY=-32.7562 EndZ=0
    g18: LineSegment StartX=-8.63967 StartY=-29.6186 StartZ=0 EndX=-44.5027 EndY=-32.7562 EndZ=0
    g19: GeomPoint X=-28.7936 Y=-5.7844 Z=0
    g20: GeomPoint X=-10.8621 Y=-4.2156 Z=0
    g21: LineSegment StartX=-9 StartY=25.5 StartZ=0 EndX=-9 EndY=-25.5 EndZ=0
    g22: LineSegment StartX=-49.9438 StartY=17.9626 StartZ=0 EndX=-47.0659 EndY=-14.9317 EndZ=0
    g23: LineSegment StartX=-66.5237 StartY=-30.6146 StartZ=0 EndX=-61.241 EndY=-27.5646 EndZ=0
    g24: LineSegment StartX=9 StartY=-25.5 StartZ=0 EndX=9 EndY=25.5 EndZ=0
    g25: LineSegment StartX=9 StartY=25.5 StartZ=0 EndX=-9 EndY=25.5 EndZ=0
    g26: LineSegment StartX=-68.6524 StartY=16.3258 StartZ=0 EndX=-50.94 EndY=17.8754 EndZ=0
    g27: LineSegment StartX=-50.94 StartY=17.8754 StartZ=0 EndX=-48.0621 EndY=-15.0189 EndZ=0
    g28: LineSegment StartX=-48.0621 StartY=-15.0189 StartZ=0 EndX=-65.7745 EndY=-16.5685 EndZ=0
    g29: LineSegment StartX=-65.7745 StartY=-16.5685 StartZ=0 EndX=-68.6524 EndY=16.3258 EndZ=0
    g30: GeomPoint X=-59.7962 Y=17.1006 Z=0
    g31: LineSegment StartX=-68.341 StartY=-15.2671 StartZ=0 EndX=-61.741 EndY=-26.6986 EndZ=0
    g32: LineSegment StartX=-61.741 StartY=-26.6986 StartZ=0 EndX=-67.0237 EndY=-29.7486 EndZ=0
    g33: LineSegment StartX=-67.0237 StartY=-29.7486 StartZ=0 EndX=-73.6237 EndY=-18.3171 EndZ=0
    g34: LineSegment StartX=-73.6237 StartY=-18.3171 StartZ=0 EndX=-68.341 EndY=-15.2671 EndZ=0
    g35: GeomPoint X=-67.4323 Y=-22.9408 Z=0
    g36: LineSegment StartX=-49.9438 StartY=17.9626 StartZ=0 EndX=-50.94 EndY=17.8754 EndZ=0
    g37: LineSegment StartX=-68.6524 StartY=16.3258 StartZ=0 EndX=-68.7395 EndY=17.322 EndZ=0
    g38: LineSegment StartX=-68.7395 StartY=17.322 StartZ=0 EndX=-69.7357 EndY=17.2349 EndZ=0
    g39: Circle CenterX=-69.7357 CenterY=17.2349 CenterZ=0 NormalX=0 NormalY=0 NormalZ=1 AngleXU=0 Radius=2
    g40: LineSegment StartX=-73.6237 StartY=-18.3171 StartZ=0 EndX=-73.1237 EndY=-19.1831 EndZ=0
    g41: ArcOfCircle CenterX=-73.1237 CenterY=-19.1831 CenterZ=0 NormalX=0 NormalY=0 NormalZ=1 AngleXU=0 Radius=1 StartAngle=2.0944 EndAngle=3.66519
    g42: LineSegment StartX=-66.8897 StartY=-31.9806 StartZ=0 EndX=-73.9897 EndY=-19.6831 EndZ=0
    g43: LineSegment StartX=-68.341 StartY=-15.2671 StartZ=0 EndX=-67.5135 EndY=-14.7893 EndZ=0
    g44: LineSegment StartX=-69.6486 StartY=16.2387 StartZ=0 EndX=-67.0173 EndY=-13.8362 EndZ=0
    g45: ArcOfCircle CenterX=-68.0135 CenterY=-13.9233 CenterZ=0 NormalX=0 NormalY=0 NormalZ=1 AngleXU=0 Radius=1 StartAngle=5.23599 EndAngle=6.37045
    g46: LineSegment StartX=-68.7395 StartY=17.322 StartZ=0 EndX=-49.0348 EndY=19.046 EndZ=0
    g47: ArcOfCircle CenterX=-48.0621 CenterY=-15.0189 CenterZ=0 NormalX=0 NormalY=0 NormalZ=1 AngleXU=0 Radius=1 StartAngle=4.79966 EndAngle=6.37045
    g48: ArcOfCircle CenterX=-61.741 CenterY=-26.6986 CenterZ=0 NormalX=0 NormalY=0 NormalZ=1 AngleXU=0 Radius=1 StartAngle=5.23599 EndAngle=6.80678
    g49: LineSegment StartX=-47.975 StartY=-16.0151 StartZ=0 EndX=-64.2877 EndY=-17.4423 EndZ=0
    g50: LineSegment StartX=-65.0666 StartY=-18.9385 StartZ=0 EndX=-60.8749 EndY=-26.1986 EndZ=0
    g51: ArcOfCircle CenterX=-64.2005 CenterY=-18.4385 CenterZ=0 NormalX=0 NormalY=0 NormalZ=1 AngleXU=0 Radius=1 StartAngle=1.65806 EndAngle=3.66519
    g52: ArcOfCircle CenterX=-66.0237 CenterY=-31.4806 CenterZ=0 NormalX=0 NormalY=0 NormalZ=1 AngleXU=0 Radius=1 StartAngle=2.0944 EndAngle=3.66519
    g53: ArcOfCircle CenterX=-68.6524 CenterY=16.3258 CenterZ=0 NormalX=0 NormalY=0 NormalZ=1 AngleXU=0 Radius=1 StartAngle=1.65806 EndAngle=3.22886
    g54: ArcOfCircle CenterX=-48.9476 CenterY=18.0498 CenterZ=0 NormalX=0 NormalY=0 NormalZ=1 AngleXU=0 Radius=1 StartAngle=1.65806 EndAngle=3.22886
  constraints (135):
    c: DistanceY(g0,g-1) = 5
    c: Horizontal(g1)
    c: Coincident(g3,g2)
    c: Coincident(g5,g4)
    c: Coincident(g6,g5)
    c: Coincident(g7,g6)
    c: Coincident(g7,g4)
    c: Perpendicular(g4,g7)
    c: Perpendicular(g5,g4)
    c: Perpendicular(g5,g6)
    c: Distance(g4) = 18
    c: Distance(g7) = 17
    c: Coincident(g9,g8)
    c: Coincident(g10,g9)
    c: Coincident(g11,g10)
    c: Coincident(g11,g8)
    c: Perpendicular(g9,g8)
    c: Perpendicular(g11,g8)
    c: Perpendicular(g10,g11)
    c: Distance(g8) = 18
    c: Distance(g11) = 34
    c: Coincident(g12,g13)
    c: Coincident(g14,g12)
    c: Horizontal(g12)
    c: Vertical(g13)
    c: Vertical(g14)
    c: Distance(g12) = 18
    c: Distance(g13) = 17
    c: Coincident(g5,g10)
    c: Angle(g14,g7) = 0.261799
    c: Angle(g11,g5) = -0.261799
    c: Coincident(g15,g13)
    c: Coincident(g15,g6)
    c: Horizontal(g15)
    c: Coincident(g16,g2)
    c: PointOnObject(g1,g16)
    c: Coincident(g17,g3)
    c: Symmetric(g2,g16,g0)
    c: Perpendicular(g2,g16)
    c: Perpendicular(g17,g3)
    c: Coincident(g18,g16)
    c: Coincident(g18,g17)
    c: Symmetric(g3,g16,g19)
    c: Symmetric(g2,g16,g20)
    c: Symmetric(g20,g19,g0)
    c: Distance(g18) = 36
    c: Perpendicular(g17,g18)
    c: Coincident(g21,g1)
    c: Vertical(g21)
    c: Symmetric(g21,g1,g-1)
    c: Distance(g21) = 51
    c: Equal(g21,g16)
    c: Angle(g21,g16) = 0.0872665
    c: Parallel(g22,g17)
    c: Coincident(g14,g6)
    c: Coincident(g24,g1)
    c: Vertical(g24)
    c: Coincident(g25,g24)
    c: Coincident(g25,g21)
    c: Horizontal(g25)
    c: Distance(g25) = 18
    c: Parallel(g23,g8)
    c: Coincident(g27,g26)
    c: Coincident(g28,g27)
    c: Coincident(g29,g28)
    c: Coincident(g29,g26)
    c: Perpendicular(g27,g26)
    c: Perpendicular(g29,g26)
    c: Perpendicular(g28,g27)
    c: Distance(g27) = 33.02
    c: Distance(g26) = 17.78
    c: Parallel(g26,g3)
    c: Symmetric(g26,g26,g30)
    c: Coincident(g32,g31)
    c: Coincident(g33,g32)
    c: Coincident(g34,g33)
    c: Perpendicular(g34,g31)
    c: Perpendicular(g33,g34)
    c: Perpendicular(g32,g33)
    c: Distance(g31) = 13.2
    c: Distance(g34) = 6.1
    c: Parallel(g23,g34)
    c: Coincident(g36,g22)
    c: Coincident(g36,g26)
    c: Distance(g36) = 1
    c: Perpendicular(g22,g36)
    c: Coincident(g37,g26)
    c: Coincident(g38,g37)
    c: Distance(g37) = 1
    c: Distance(g38) = 1
    c: Perpendicular(g26,g37)
    c: Perpendicular(g38,g37)
    c: Coincident(g39,g38)
    c: Radius(g39) = 2
    c: Coincident(g40,g33)
    c: Distance(g40) = 1
    c: Coincident(g41,g40)
    c: Coincident(g41,g33)
    c: PointOnObject(g40,g33)
    c: Parallel(g29,g44)
    c: Tangent(g45,g44) = 1.5708
    c: Tangent(g45,g43) = -1.5708
    c: Radius(g45) = 1
    c: Coincident(g46,g37)
    c: Coincident(g31,g34)
    c: Coincident(g43,g31)
    c: Parallel(g43,g34)
    c: Symmetric(g40,g31,g35)
    c: Coincident(g48,g31)
    c: Parallel(g49,g28)
    c: Tangent(g51,g49) = -1.5708
    c: Tangent(g51,g50) = -1.5708
    c: Radius(g51) = 1
    c: Radius(g48) = 1
    c: Tangent(g50,g48) = 1.5708
    c: Parallel(g50,g31)
    c: Tangent(g22,g47) = 1.5708
    c: Tangent(g49,g47) = 1.5708
    c: PointOnObject(g17,g11)
    c: PointOnObject(g12,g18)
    c: Coincident(g47,g27)
    c: Tangent(g41,g42) = 1.5708
    c: Coincident(g52,g8)
    c: Radius(g52) = 1
    c: Tangent(g52,g23) = 1.5708
    c: Tangent(g52,g42) = 1.5708
    c: Tangent(g48,g23) = -1.5708
    c: Parallel(g33,g42)
    c: Coincident(g53,g26)
    c: Coincident(g53,g37)
    c: Tangent(g53,g44) = -1.5708
    c: Coincident(g54,g3)
    c: Tangent(g54,g46) = 1.5708
    c: Tangent(g54,g22) = -1.5708
    c: Radius(g54) = 1
